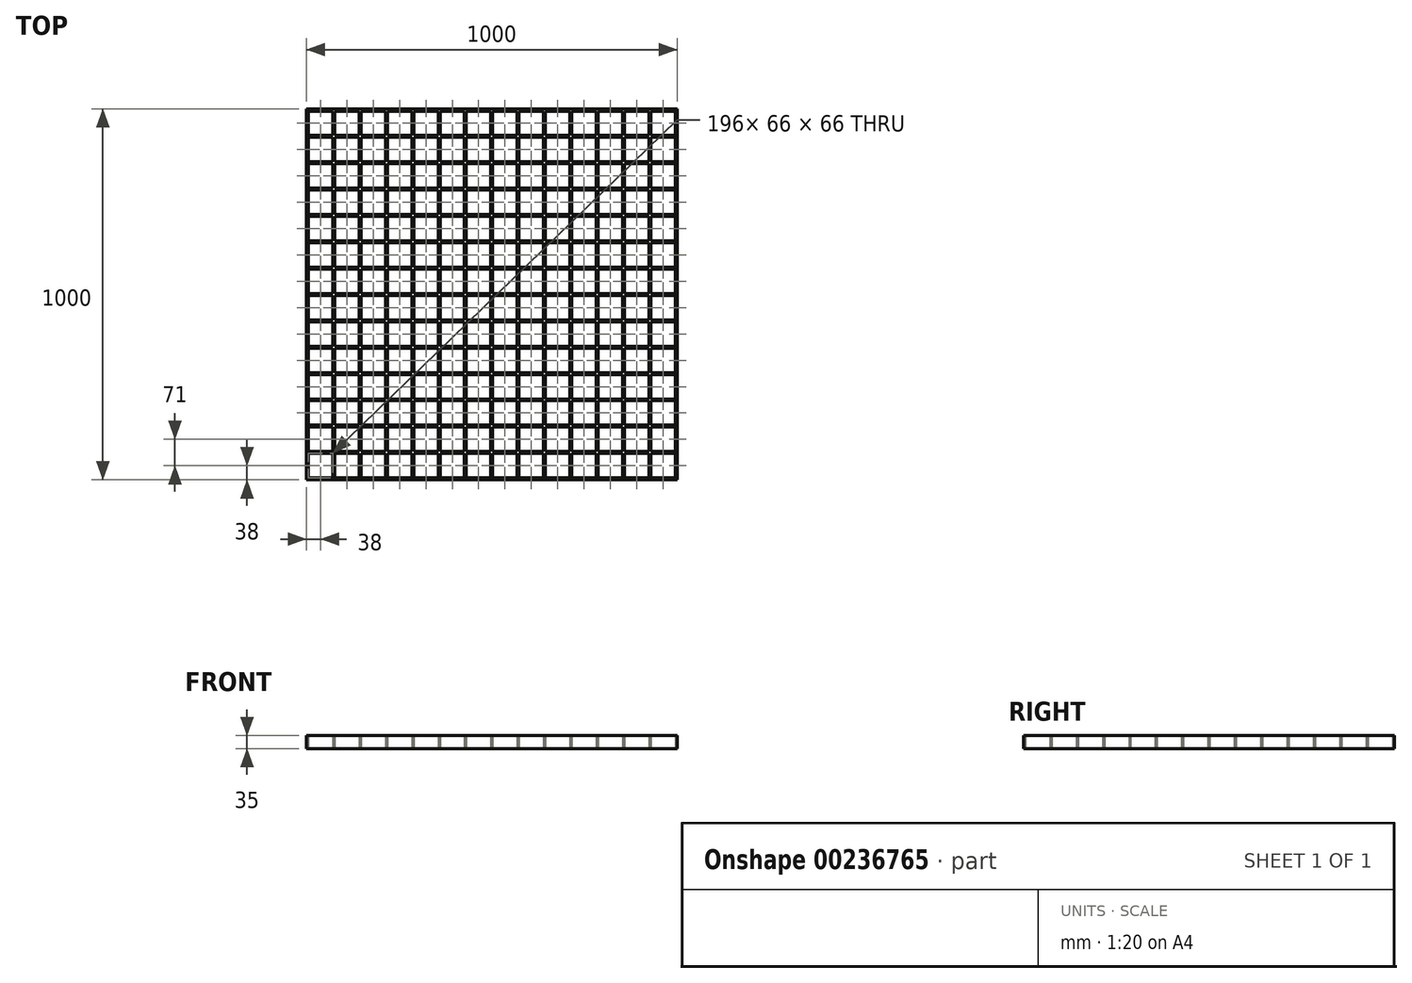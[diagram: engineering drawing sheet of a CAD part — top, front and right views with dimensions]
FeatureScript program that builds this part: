
annotation { "Feature Type Name" : "Feature", "Feature Type Description" : "" }
export const myFeature = defineFeature(function(context is Context, id is Id, definition is map)
    precondition{}
    {
        {
            var Q0;
            Q0=qCreatedBy(makeId("Top.planeOp"),FACE);
            var sketch = newSketch(context, id + "F0", { "sketchPlane" : qUnion([Q0])});
            skLineSegment(sketch, "E0.bottom", {"start": v(0, 0) * mm, "end": v(1000, 0) * mm});
            skLineSegment(sketch, "E0.top", {"start": v(0, 1000) * mm, "end": v(1000, 1000) * mm});
            skLineSegment(sketch, "E0.left", {"start": v(0, 0) * mm, "end": v(0, 1000) * mm});
            skLineSegment(sketch, "E0.right", {"start": v(1000, 0) * mm, "end": v(1000, 1000) * mm});
            skLineSegment(sketch, "E1.bottom", {"start": v(5, 5) * mm, "end": v(71, 5) * mm});
            skLineSegment(sketch, "E1.top", {"start": v(5, 71) * mm, "end": v(71, 71) * mm});
            skLineSegment(sketch, "E1.left", {"start": v(5, 5) * mm, "end": v(5, 71) * mm});
            skLineSegment(sketch, "E1.right", {"start": v(71, 5) * mm, "end": v(71, 71) * mm});
            skLineSegment(sketch, "E2.0.1.0", {"start": v(5, 142) * mm, "end": v(71, 142) * mm});
            skLineSegment(sketch, "E2.0.1.1", {"start": v(5, 76) * mm, "end": v(5, 142) * mm});
            skLineSegment(sketch, "E2.0.1.2", {"start": v(5, 76) * mm, "end": v(71, 76) * mm});
            skLineSegment(sketch, "E2.0.1.3", {"start": v(71, 76) * mm, "end": v(71, 142) * mm});
            skLineSegment(sketch, "E2.0.2.0", {"start": v(5, 213) * mm, "end": v(71, 213) * mm});
            skLineSegment(sketch, "E2.0.2.1", {"start": v(5, 147) * mm, "end": v(5, 213) * mm});
            skLineSegment(sketch, "E2.0.2.2", {"start": v(5, 147) * mm, "end": v(71, 147) * mm});
            skLineSegment(sketch, "E2.0.2.3", {"start": v(71, 147) * mm, "end": v(71, 213) * mm});
            skLineSegment(sketch, "E2.0.3.0", {"start": v(5, 284) * mm, "end": v(71, 284) * mm});
            skLineSegment(sketch, "E2.0.3.1", {"start": v(5, 218) * mm, "end": v(5, 284) * mm});
            skLineSegment(sketch, "E2.0.3.2", {"start": v(5, 218) * mm, "end": v(71, 218) * mm});
            skLineSegment(sketch, "E2.0.3.3", {"start": v(71, 218) * mm, "end": v(71, 284) * mm});
            skLineSegment(sketch, "E2.0.4.0", {"start": v(5, 355) * mm, "end": v(71, 355) * mm});
            skLineSegment(sketch, "E2.0.4.1", {"start": v(5, 289) * mm, "end": v(5, 355) * mm});
            skLineSegment(sketch, "E2.0.4.2", {"start": v(5, 289) * mm, "end": v(71, 289) * mm});
            skLineSegment(sketch, "E2.0.4.3", {"start": v(71, 289) * mm, "end": v(71, 355) * mm});
            skLineSegment(sketch, "E2.0.5.0", {"start": v(5, 426) * mm, "end": v(71, 426) * mm});
            skLineSegment(sketch, "E2.0.5.1", {"start": v(5, 360) * mm, "end": v(5, 426) * mm});
            skLineSegment(sketch, "E2.0.5.2", {"start": v(5, 360) * mm, "end": v(71, 360) * mm});
            skLineSegment(sketch, "E2.0.5.3", {"start": v(71, 360) * mm, "end": v(71, 426) * mm});
            skLineSegment(sketch, "E2.0.6.0", {"start": v(5, 497) * mm, "end": v(71, 497) * mm});
            skLineSegment(sketch, "E2.0.6.1", {"start": v(5, 431) * mm, "end": v(5, 497) * mm});
            skLineSegment(sketch, "E2.0.6.2", {"start": v(5, 431) * mm, "end": v(71, 431) * mm});
            skLineSegment(sketch, "E2.0.6.3", {"start": v(71, 431) * mm, "end": v(71, 497) * mm});
            skLineSegment(sketch, "E2.0.7.0", {"start": v(5, 568) * mm, "end": v(71, 568) * mm});
            skLineSegment(sketch, "E2.0.7.1", {"start": v(5, 502) * mm, "end": v(5, 568) * mm});
            skLineSegment(sketch, "E2.0.7.2", {"start": v(5, 502) * mm, "end": v(71, 502) * mm});
            skLineSegment(sketch, "E2.0.7.3", {"start": v(71, 502) * mm, "end": v(71, 568) * mm});
            skLineSegment(sketch, "E2.0.8.0", {"start": v(5, 639) * mm, "end": v(71, 639) * mm});
            skLineSegment(sketch, "E2.0.8.1", {"start": v(5, 573) * mm, "end": v(5, 639) * mm});
            skLineSegment(sketch, "E2.0.8.2", {"start": v(5, 573) * mm, "end": v(71, 573) * mm});
            skLineSegment(sketch, "E2.0.8.3", {"start": v(71, 573) * mm, "end": v(71, 639) * mm});
            skLineSegment(sketch, "E2.0.9.0", {"start": v(5, 710) * mm, "end": v(71, 710) * mm});
            skLineSegment(sketch, "E2.0.9.1", {"start": v(5, 644) * mm, "end": v(5, 710) * mm});
            skLineSegment(sketch, "E2.0.9.2", {"start": v(5, 644) * mm, "end": v(71, 644) * mm});
            skLineSegment(sketch, "E2.0.9.3", {"start": v(71, 644) * mm, "end": v(71, 710) * mm});
            skLineSegment(sketch, "E2.0.10.0", {"start": v(5, 781) * mm, "end": v(71, 781) * mm});
            skLineSegment(sketch, "E2.0.10.1", {"start": v(5, 715) * mm, "end": v(5, 781) * mm});
            skLineSegment(sketch, "E2.0.10.2", {"start": v(5, 715) * mm, "end": v(71, 715) * mm});
            skLineSegment(sketch, "E2.0.10.3", {"start": v(71, 715) * mm, "end": v(71, 781) * mm});
            skLineSegment(sketch, "E2.0.11.0", {"start": v(5, 852) * mm, "end": v(71, 852) * mm});
            skLineSegment(sketch, "E2.0.11.1", {"start": v(5, 786) * mm, "end": v(5, 852) * mm});
            skLineSegment(sketch, "E2.0.11.2", {"start": v(5, 786) * mm, "end": v(71, 786) * mm});
            skLineSegment(sketch, "E2.0.11.3", {"start": v(71, 786) * mm, "end": v(71, 852) * mm});
            skLineSegment(sketch, "E2.0.12.0", {"start": v(5, 923) * mm, "end": v(71, 923) * mm});
            skLineSegment(sketch, "E2.0.12.1", {"start": v(5, 857) * mm, "end": v(5, 923) * mm});
            skLineSegment(sketch, "E2.0.12.2", {"start": v(5, 857) * mm, "end": v(71, 857) * mm});
            skLineSegment(sketch, "E2.0.12.3", {"start": v(71, 857) * mm, "end": v(71, 923) * mm});
            skLineSegment(sketch, "E2.0.13.0", {"start": v(5, 994) * mm, "end": v(71, 994) * mm});
            skLineSegment(sketch, "E2.0.13.1", {"start": v(5, 928) * mm, "end": v(5, 994) * mm});
            skLineSegment(sketch, "E2.0.13.2", {"start": v(5, 928) * mm, "end": v(71, 928) * mm});
            skLineSegment(sketch, "E2.0.13.3", {"start": v(71, 928) * mm, "end": v(71, 994) * mm});
            skLineSegment(sketch, "E2.1.0.0", {"start": v(76, 71) * mm, "end": v(142, 71) * mm});
            skLineSegment(sketch, "E2.1.0.1", {"start": v(76, 5) * mm, "end": v(76, 71) * mm});
            skLineSegment(sketch, "E2.1.0.2", {"start": v(76, 5) * mm, "end": v(142, 5) * mm});
            skLineSegment(sketch, "E2.1.0.3", {"start": v(142, 5) * mm, "end": v(142, 71) * mm});
            skLineSegment(sketch, "E2.1.1.0", {"start": v(76, 142) * mm, "end": v(142, 142) * mm});
            skLineSegment(sketch, "E2.1.1.1", {"start": v(76, 76) * mm, "end": v(76, 142) * mm});
            skLineSegment(sketch, "E2.1.1.2", {"start": v(76, 76) * mm, "end": v(142, 76) * mm});
            skLineSegment(sketch, "E2.1.1.3", {"start": v(142, 76) * mm, "end": v(142, 142) * mm});
            skLineSegment(sketch, "E2.1.2.0", {"start": v(76, 213) * mm, "end": v(142, 213) * mm});
            skLineSegment(sketch, "E2.1.2.1", {"start": v(76, 147) * mm, "end": v(76, 213) * mm});
            skLineSegment(sketch, "E2.1.2.2", {"start": v(76, 147) * mm, "end": v(142, 147) * mm});
            skLineSegment(sketch, "E2.1.2.3", {"start": v(142, 147) * mm, "end": v(142, 213) * mm});
            skLineSegment(sketch, "E2.1.3.0", {"start": v(76, 284) * mm, "end": v(142, 284) * mm});
            skLineSegment(sketch, "E2.1.3.1", {"start": v(76, 218) * mm, "end": v(76, 284) * mm});
            skLineSegment(sketch, "E2.1.3.2", {"start": v(76, 218) * mm, "end": v(142, 218) * mm});
            skLineSegment(sketch, "E2.1.3.3", {"start": v(142, 218) * mm, "end": v(142, 284) * mm});
            skLineSegment(sketch, "E2.1.4.0", {"start": v(76, 355) * mm, "end": v(142, 355) * mm});
            skLineSegment(sketch, "E2.1.4.1", {"start": v(76, 289) * mm, "end": v(76, 355) * mm});
            skLineSegment(sketch, "E2.1.4.2", {"start": v(76, 289) * mm, "end": v(142, 289) * mm});
            skLineSegment(sketch, "E2.1.4.3", {"start": v(142, 289) * mm, "end": v(142, 355) * mm});
            skLineSegment(sketch, "E2.1.5.0", {"start": v(76, 426) * mm, "end": v(142, 426) * mm});
            skLineSegment(sketch, "E2.1.5.1", {"start": v(76, 360) * mm, "end": v(76, 426) * mm});
            skLineSegment(sketch, "E2.1.5.2", {"start": v(76, 360) * mm, "end": v(142, 360) * mm});
            skLineSegment(sketch, "E2.1.5.3", {"start": v(142, 360) * mm, "end": v(142, 426) * mm});
            skLineSegment(sketch, "E2.1.6.0", {"start": v(76, 497) * mm, "end": v(142, 497) * mm});
            skLineSegment(sketch, "E2.1.6.1", {"start": v(76, 431) * mm, "end": v(76, 497) * mm});
            skLineSegment(sketch, "E2.1.6.2", {"start": v(76, 431) * mm, "end": v(142, 431) * mm});
            skLineSegment(sketch, "E2.1.6.3", {"start": v(142, 431) * mm, "end": v(142, 497) * mm});
            skLineSegment(sketch, "E2.1.7.0", {"start": v(76, 568) * mm, "end": v(142, 568) * mm});
            skLineSegment(sketch, "E2.1.7.1", {"start": v(76, 502) * mm, "end": v(76, 568) * mm});
            skLineSegment(sketch, "E2.1.7.2", {"start": v(76, 502) * mm, "end": v(142, 502) * mm});
            skLineSegment(sketch, "E2.1.7.3", {"start": v(142, 502) * mm, "end": v(142, 568) * mm});
            skLineSegment(sketch, "E2.1.8.0", {"start": v(76, 639) * mm, "end": v(142, 639) * mm});
            skLineSegment(sketch, "E2.1.8.1", {"start": v(76, 573) * mm, "end": v(76, 639) * mm});
            skLineSegment(sketch, "E2.1.8.2", {"start": v(76, 573) * mm, "end": v(142, 573) * mm});
            skLineSegment(sketch, "E2.1.8.3", {"start": v(142, 573) * mm, "end": v(142, 639) * mm});
            skLineSegment(sketch, "E2.1.9.0", {"start": v(76, 710) * mm, "end": v(142, 710) * mm});
            skLineSegment(sketch, "E2.1.9.1", {"start": v(76, 644) * mm, "end": v(76, 710) * mm});
            skLineSegment(sketch, "E2.1.9.2", {"start": v(76, 644) * mm, "end": v(142, 644) * mm});
            skLineSegment(sketch, "E2.1.9.3", {"start": v(142, 644) * mm, "end": v(142, 710) * mm});
            skLineSegment(sketch, "E2.1.10.0", {"start": v(76, 781) * mm, "end": v(142, 781) * mm});
            skLineSegment(sketch, "E2.1.10.1", {"start": v(76, 715) * mm, "end": v(76, 781) * mm});
            skLineSegment(sketch, "E2.1.10.2", {"start": v(76, 715) * mm, "end": v(142, 715) * mm});
            skLineSegment(sketch, "E2.1.10.3", {"start": v(142, 715) * mm, "end": v(142, 781) * mm});
            skLineSegment(sketch, "E2.1.11.0", {"start": v(76, 852) * mm, "end": v(142, 852) * mm});
            skLineSegment(sketch, "E2.1.11.1", {"start": v(76, 786) * mm, "end": v(76, 852) * mm});
            skLineSegment(sketch, "E2.1.11.2", {"start": v(76, 786) * mm, "end": v(142, 786) * mm});
            skLineSegment(sketch, "E2.1.11.3", {"start": v(142, 786) * mm, "end": v(142, 852) * mm});
            skLineSegment(sketch, "E2.1.12.0", {"start": v(76, 923) * mm, "end": v(142, 923) * mm});
            skLineSegment(sketch, "E2.1.12.1", {"start": v(76, 857) * mm, "end": v(76, 923) * mm});
            skLineSegment(sketch, "E2.1.12.2", {"start": v(76, 857) * mm, "end": v(142, 857) * mm});
            skLineSegment(sketch, "E2.1.12.3", {"start": v(142, 857) * mm, "end": v(142, 923) * mm});
            skLineSegment(sketch, "E2.1.13.0", {"start": v(76, 994) * mm, "end": v(142, 994) * mm});
            skLineSegment(sketch, "E2.1.13.1", {"start": v(76, 928) * mm, "end": v(76, 994) * mm});
            skLineSegment(sketch, "E2.1.13.2", {"start": v(76, 928) * mm, "end": v(142, 928) * mm});
            skLineSegment(sketch, "E2.1.13.3", {"start": v(142, 928) * mm, "end": v(142, 994) * mm});
            skLineSegment(sketch, "E2.2.0.0", {"start": v(147, 71) * mm, "end": v(213, 71) * mm});
            skLineSegment(sketch, "E2.2.0.1", {"start": v(147, 5) * mm, "end": v(147, 71) * mm});
            skLineSegment(sketch, "E2.2.0.2", {"start": v(147, 5) * mm, "end": v(213, 5) * mm});
            skLineSegment(sketch, "E2.2.0.3", {"start": v(213, 5) * mm, "end": v(213, 71) * mm});
            skLineSegment(sketch, "E2.2.1.0", {"start": v(147, 142) * mm, "end": v(213, 142) * mm});
            skLineSegment(sketch, "E2.2.1.1", {"start": v(147, 76) * mm, "end": v(147, 142) * mm});
            skLineSegment(sketch, "E2.2.1.2", {"start": v(147, 76) * mm, "end": v(213, 76) * mm});
            skLineSegment(sketch, "E2.2.1.3", {"start": v(213, 76) * mm, "end": v(213, 142) * mm});
            skLineSegment(sketch, "E2.2.2.0", {"start": v(147, 213) * mm, "end": v(213, 213) * mm});
            skLineSegment(sketch, "E2.2.2.1", {"start": v(147, 147) * mm, "end": v(147, 213) * mm});
            skLineSegment(sketch, "E2.2.2.2", {"start": v(147, 147) * mm, "end": v(213, 147) * mm});
            skLineSegment(sketch, "E2.2.2.3", {"start": v(213, 147) * mm, "end": v(213, 213) * mm});
            skLineSegment(sketch, "E2.2.3.0", {"start": v(147, 284) * mm, "end": v(213, 284) * mm});
            skLineSegment(sketch, "E2.2.3.1", {"start": v(147, 218) * mm, "end": v(147, 284) * mm});
            skLineSegment(sketch, "E2.2.3.2", {"start": v(147, 218) * mm, "end": v(213, 218) * mm});
            skLineSegment(sketch, "E2.2.3.3", {"start": v(213, 218) * mm, "end": v(213, 284) * mm});
            skLineSegment(sketch, "E2.2.4.0", {"start": v(147, 355) * mm, "end": v(213, 355) * mm});
            skLineSegment(sketch, "E2.2.4.1", {"start": v(147, 289) * mm, "end": v(147, 355) * mm});
            skLineSegment(sketch, "E2.2.4.2", {"start": v(147, 289) * mm, "end": v(213, 289) * mm});
            skLineSegment(sketch, "E2.2.4.3", {"start": v(213, 289) * mm, "end": v(213, 355) * mm});
            skLineSegment(sketch, "E2.2.5.0", {"start": v(147, 426) * mm, "end": v(213, 426) * mm});
            skLineSegment(sketch, "E2.2.5.1", {"start": v(147, 360) * mm, "end": v(147, 426) * mm});
            skLineSegment(sketch, "E2.2.5.2", {"start": v(147, 360) * mm, "end": v(213, 360) * mm});
            skLineSegment(sketch, "E2.2.5.3", {"start": v(213, 360) * mm, "end": v(213, 426) * mm});
            skLineSegment(sketch, "E2.2.6.0", {"start": v(147, 497) * mm, "end": v(213, 497) * mm});
            skLineSegment(sketch, "E2.2.6.1", {"start": v(147, 431) * mm, "end": v(147, 497) * mm});
            skLineSegment(sketch, "E2.2.6.2", {"start": v(147, 431) * mm, "end": v(213, 431) * mm});
            skLineSegment(sketch, "E2.2.6.3", {"start": v(213, 431) * mm, "end": v(213, 497) * mm});
            skLineSegment(sketch, "E2.2.7.0", {"start": v(147, 568) * mm, "end": v(213, 568) * mm});
            skLineSegment(sketch, "E2.2.7.1", {"start": v(147, 502) * mm, "end": v(147, 568) * mm});
            skLineSegment(sketch, "E2.2.7.2", {"start": v(147, 502) * mm, "end": v(213, 502) * mm});
            skLineSegment(sketch, "E2.2.7.3", {"start": v(213, 502) * mm, "end": v(213, 568) * mm});
            skLineSegment(sketch, "E2.2.8.0", {"start": v(147, 639) * mm, "end": v(213, 639) * mm});
            skLineSegment(sketch, "E2.2.8.1", {"start": v(147, 573) * mm, "end": v(147, 639) * mm});
            skLineSegment(sketch, "E2.2.8.2", {"start": v(147, 573) * mm, "end": v(213, 573) * mm});
            skLineSegment(sketch, "E2.2.8.3", {"start": v(213, 573) * mm, "end": v(213, 639) * mm});
            skLineSegment(sketch, "E2.2.9.0", {"start": v(147, 710) * mm, "end": v(213, 710) * mm});
            skLineSegment(sketch, "E2.2.9.1", {"start": v(147, 644) * mm, "end": v(147, 710) * mm});
            skLineSegment(sketch, "E2.2.9.2", {"start": v(147, 644) * mm, "end": v(213, 644) * mm});
            skLineSegment(sketch, "E2.2.9.3", {"start": v(213, 644) * mm, "end": v(213, 710) * mm});
            skLineSegment(sketch, "E2.2.10.0", {"start": v(147, 781) * mm, "end": v(213, 781) * mm});
            skLineSegment(sketch, "E2.2.10.1", {"start": v(147, 715) * mm, "end": v(147, 781) * mm});
            skLineSegment(sketch, "E2.2.10.2", {"start": v(147, 715) * mm, "end": v(213, 715) * mm});
            skLineSegment(sketch, "E2.2.10.3", {"start": v(213, 715) * mm, "end": v(213, 781) * mm});
            skLineSegment(sketch, "E2.2.11.0", {"start": v(147, 852) * mm, "end": v(213, 852) * mm});
            skLineSegment(sketch, "E2.2.11.1", {"start": v(147, 786) * mm, "end": v(147, 852) * mm});
            skLineSegment(sketch, "E2.2.11.2", {"start": v(147, 786) * mm, "end": v(213, 786) * mm});
            skLineSegment(sketch, "E2.2.11.3", {"start": v(213, 786) * mm, "end": v(213, 852) * mm});
            skLineSegment(sketch, "E2.2.12.0", {"start": v(147, 923) * mm, "end": v(213, 923) * mm});
            skLineSegment(sketch, "E2.2.12.1", {"start": v(147, 857) * mm, "end": v(147, 923) * mm});
            skLineSegment(sketch, "E2.2.12.2", {"start": v(147, 857) * mm, "end": v(213, 857) * mm});
            skLineSegment(sketch, "E2.2.12.3", {"start": v(213, 857) * mm, "end": v(213, 923) * mm});
            skLineSegment(sketch, "E2.2.13.0", {"start": v(147, 994) * mm, "end": v(213, 994) * mm});
            skLineSegment(sketch, "E2.2.13.1", {"start": v(147, 928) * mm, "end": v(147, 994) * mm});
            skLineSegment(sketch, "E2.2.13.2", {"start": v(147, 928) * mm, "end": v(213, 928) * mm});
            skLineSegment(sketch, "E2.2.13.3", {"start": v(213, 928) * mm, "end": v(213, 994) * mm});
            skLineSegment(sketch, "E2.3.0.0", {"start": v(218, 71) * mm, "end": v(284, 71) * mm});
            skLineSegment(sketch, "E2.3.0.1", {"start": v(218, 5) * mm, "end": v(218, 71) * mm});
            skLineSegment(sketch, "E2.3.0.2", {"start": v(218, 5) * mm, "end": v(284, 5) * mm});
            skLineSegment(sketch, "E2.3.0.3", {"start": v(284, 5) * mm, "end": v(284, 71) * mm});
            skLineSegment(sketch, "E2.3.1.0", {"start": v(218, 142) * mm, "end": v(284, 142) * mm});
            skLineSegment(sketch, "E2.3.1.1", {"start": v(218, 76) * mm, "end": v(218, 142) * mm});
            skLineSegment(sketch, "E2.3.1.2", {"start": v(218, 76) * mm, "end": v(284, 76) * mm});
            skLineSegment(sketch, "E2.3.1.3", {"start": v(284, 76) * mm, "end": v(284, 142) * mm});
            skLineSegment(sketch, "E2.3.2.0", {"start": v(218, 213) * mm, "end": v(284, 213) * mm});
            skLineSegment(sketch, "E2.3.2.1", {"start": v(218, 147) * mm, "end": v(218, 213) * mm});
            skLineSegment(sketch, "E2.3.2.2", {"start": v(218, 147) * mm, "end": v(284, 147) * mm});
            skLineSegment(sketch, "E2.3.2.3", {"start": v(284, 147) * mm, "end": v(284, 213) * mm});
            skLineSegment(sketch, "E2.3.3.0", {"start": v(218, 284) * mm, "end": v(284, 284) * mm});
            skLineSegment(sketch, "E2.3.3.1", {"start": v(218, 218) * mm, "end": v(218, 284) * mm});
            skLineSegment(sketch, "E2.3.3.2", {"start": v(218, 218) * mm, "end": v(284, 218) * mm});
            skLineSegment(sketch, "E2.3.3.3", {"start": v(284, 218) * mm, "end": v(284, 284) * mm});
            skLineSegment(sketch, "E2.3.4.0", {"start": v(218, 355) * mm, "end": v(284, 355) * mm});
            skLineSegment(sketch, "E2.3.4.1", {"start": v(218, 289) * mm, "end": v(218, 355) * mm});
            skLineSegment(sketch, "E2.3.4.2", {"start": v(218, 289) * mm, "end": v(284, 289) * mm});
            skLineSegment(sketch, "E2.3.4.3", {"start": v(284, 289) * mm, "end": v(284, 355) * mm});
            skLineSegment(sketch, "E2.3.5.0", {"start": v(218, 426) * mm, "end": v(284, 426) * mm});
            skLineSegment(sketch, "E2.3.5.1", {"start": v(218, 360) * mm, "end": v(218, 426) * mm});
            skLineSegment(sketch, "E2.3.5.2", {"start": v(218, 360) * mm, "end": v(284, 360) * mm});
            skLineSegment(sketch, "E2.3.5.3", {"start": v(284, 360) * mm, "end": v(284, 426) * mm});
            skLineSegment(sketch, "E2.3.6.0", {"start": v(218, 497) * mm, "end": v(284, 497) * mm});
            skLineSegment(sketch, "E2.3.6.1", {"start": v(218, 431) * mm, "end": v(218, 497) * mm});
            skLineSegment(sketch, "E2.3.6.2", {"start": v(218, 431) * mm, "end": v(284, 431) * mm});
            skLineSegment(sketch, "E2.3.6.3", {"start": v(284, 431) * mm, "end": v(284, 497) * mm});
            skLineSegment(sketch, "E2.3.7.0", {"start": v(218, 568) * mm, "end": v(284, 568) * mm});
            skLineSegment(sketch, "E2.3.7.1", {"start": v(218, 502) * mm, "end": v(218, 568) * mm});
            skLineSegment(sketch, "E2.3.7.2", {"start": v(218, 502) * mm, "end": v(284, 502) * mm});
            skLineSegment(sketch, "E2.3.7.3", {"start": v(284, 502) * mm, "end": v(284, 568) * mm});
            skLineSegment(sketch, "E2.3.8.0", {"start": v(218, 639) * mm, "end": v(284, 639) * mm});
            skLineSegment(sketch, "E2.3.8.1", {"start": v(218, 573) * mm, "end": v(218, 639) * mm});
            skLineSegment(sketch, "E2.3.8.2", {"start": v(218, 573) * mm, "end": v(284, 573) * mm});
            skLineSegment(sketch, "E2.3.8.3", {"start": v(284, 573) * mm, "end": v(284, 639) * mm});
            skLineSegment(sketch, "E2.3.9.0", {"start": v(218, 710) * mm, "end": v(284, 710) * mm});
            skLineSegment(sketch, "E2.3.9.1", {"start": v(218, 644) * mm, "end": v(218, 710) * mm});
            skLineSegment(sketch, "E2.3.9.2", {"start": v(218, 644) * mm, "end": v(284, 644) * mm});
            skLineSegment(sketch, "E2.3.9.3", {"start": v(284, 644) * mm, "end": v(284, 710) * mm});
            skLineSegment(sketch, "E2.3.10.0", {"start": v(218, 781) * mm, "end": v(284, 781) * mm});
            skLineSegment(sketch, "E2.3.10.1", {"start": v(218, 715) * mm, "end": v(218, 781) * mm});
            skLineSegment(sketch, "E2.3.10.2", {"start": v(218, 715) * mm, "end": v(284, 715) * mm});
            skLineSegment(sketch, "E2.3.10.3", {"start": v(284, 715) * mm, "end": v(284, 781) * mm});
            skLineSegment(sketch, "E2.3.11.0", {"start": v(218, 852) * mm, "end": v(284, 852) * mm});
            skLineSegment(sketch, "E2.3.11.1", {"start": v(218, 786) * mm, "end": v(218, 852) * mm});
            skLineSegment(sketch, "E2.3.11.2", {"start": v(218, 786) * mm, "end": v(284, 786) * mm});
            skLineSegment(sketch, "E2.3.11.3", {"start": v(284, 786) * mm, "end": v(284, 852) * mm});
            skLineSegment(sketch, "E2.3.12.0", {"start": v(218, 923) * mm, "end": v(284, 923) * mm});
            skLineSegment(sketch, "E2.3.12.1", {"start": v(218, 857) * mm, "end": v(218, 923) * mm});
            skLineSegment(sketch, "E2.3.12.2", {"start": v(218, 857) * mm, "end": v(284, 857) * mm});
            skLineSegment(sketch, "E2.3.12.3", {"start": v(284, 857) * mm, "end": v(284, 923) * mm});
            skLineSegment(sketch, "E2.3.13.0", {"start": v(218, 994) * mm, "end": v(284, 994) * mm});
            skLineSegment(sketch, "E2.3.13.1", {"start": v(218, 928) * mm, "end": v(218, 994) * mm});
            skLineSegment(sketch, "E2.3.13.2", {"start": v(218, 928) * mm, "end": v(284, 928) * mm});
            skLineSegment(sketch, "E2.3.13.3", {"start": v(284, 928) * mm, "end": v(284, 994) * mm});
            skLineSegment(sketch, "E2.4.0.0", {"start": v(289, 71) * mm, "end": v(355, 71) * mm});
            skLineSegment(sketch, "E2.4.0.1", {"start": v(289, 5) * mm, "end": v(289, 71) * mm});
            skLineSegment(sketch, "E2.4.0.2", {"start": v(289, 5) * mm, "end": v(355, 5) * mm});
            skLineSegment(sketch, "E2.4.0.3", {"start": v(355, 5) * mm, "end": v(355, 71) * mm});
            skLineSegment(sketch, "E2.4.1.0", {"start": v(289, 142) * mm, "end": v(355, 142) * mm});
            skLineSegment(sketch, "E2.4.1.1", {"start": v(289, 76) * mm, "end": v(289, 142) * mm});
            skLineSegment(sketch, "E2.4.1.2", {"start": v(289, 76) * mm, "end": v(355, 76) * mm});
            skLineSegment(sketch, "E2.4.1.3", {"start": v(355, 76) * mm, "end": v(355, 142) * mm});
            skLineSegment(sketch, "E2.4.2.0", {"start": v(289, 213) * mm, "end": v(355, 213) * mm});
            skLineSegment(sketch, "E2.4.2.1", {"start": v(289, 147) * mm, "end": v(289, 213) * mm});
            skLineSegment(sketch, "E2.4.2.2", {"start": v(289, 147) * mm, "end": v(355, 147) * mm});
            skLineSegment(sketch, "E2.4.2.3", {"start": v(355, 147) * mm, "end": v(355, 213) * mm});
            skLineSegment(sketch, "E2.4.3.0", {"start": v(289, 284) * mm, "end": v(355, 284) * mm});
            skLineSegment(sketch, "E2.4.3.1", {"start": v(289, 218) * mm, "end": v(289, 284) * mm});
            skLineSegment(sketch, "E2.4.3.2", {"start": v(289, 218) * mm, "end": v(355, 218) * mm});
            skLineSegment(sketch, "E2.4.3.3", {"start": v(355, 218) * mm, "end": v(355, 284) * mm});
            skLineSegment(sketch, "E2.4.4.0", {"start": v(289, 355) * mm, "end": v(355, 355) * mm});
            skLineSegment(sketch, "E2.4.4.1", {"start": v(289, 289) * mm, "end": v(289, 355) * mm});
            skLineSegment(sketch, "E2.4.4.2", {"start": v(289, 289) * mm, "end": v(355, 289) * mm});
            skLineSegment(sketch, "E2.4.4.3", {"start": v(355, 289) * mm, "end": v(355, 355) * mm});
            skLineSegment(sketch, "E2.4.5.0", {"start": v(289, 426) * mm, "end": v(355, 426) * mm});
            skLineSegment(sketch, "E2.4.5.1", {"start": v(289, 360) * mm, "end": v(289, 426) * mm});
            skLineSegment(sketch, "E2.4.5.2", {"start": v(289, 360) * mm, "end": v(355, 360) * mm});
            skLineSegment(sketch, "E2.4.5.3", {"start": v(355, 360) * mm, "end": v(355, 426) * mm});
            skLineSegment(sketch, "E2.4.6.0", {"start": v(289, 497) * mm, "end": v(355, 497) * mm});
            skLineSegment(sketch, "E2.4.6.1", {"start": v(289, 431) * mm, "end": v(289, 497) * mm});
            skLineSegment(sketch, "E2.4.6.2", {"start": v(289, 431) * mm, "end": v(355, 431) * mm});
            skLineSegment(sketch, "E2.4.6.3", {"start": v(355, 431) * mm, "end": v(355, 497) * mm});
            skLineSegment(sketch, "E2.4.7.0", {"start": v(289, 568) * mm, "end": v(355, 568) * mm});
            skLineSegment(sketch, "E2.4.7.1", {"start": v(289, 502) * mm, "end": v(289, 568) * mm});
            skLineSegment(sketch, "E2.4.7.2", {"start": v(289, 502) * mm, "end": v(355, 502) * mm});
            skLineSegment(sketch, "E2.4.7.3", {"start": v(355, 502) * mm, "end": v(355, 568) * mm});
            skLineSegment(sketch, "E2.4.8.0", {"start": v(289, 639) * mm, "end": v(355, 639) * mm});
            skLineSegment(sketch, "E2.4.8.1", {"start": v(289, 573) * mm, "end": v(289, 639) * mm});
            skLineSegment(sketch, "E2.4.8.2", {"start": v(289, 573) * mm, "end": v(355, 573) * mm});
            skLineSegment(sketch, "E2.4.8.3", {"start": v(355, 573) * mm, "end": v(355, 639) * mm});
            skLineSegment(sketch, "E2.4.9.0", {"start": v(289, 710) * mm, "end": v(355, 710) * mm});
            skLineSegment(sketch, "E2.4.9.1", {"start": v(289, 644) * mm, "end": v(289, 710) * mm});
            skLineSegment(sketch, "E2.4.9.2", {"start": v(289, 644) * mm, "end": v(355, 644) * mm});
            skLineSegment(sketch, "E2.4.9.3", {"start": v(355, 644) * mm, "end": v(355, 710) * mm});
            skLineSegment(sketch, "E2.4.10.0", {"start": v(289, 781) * mm, "end": v(355, 781) * mm});
            skLineSegment(sketch, "E2.4.10.1", {"start": v(289, 715) * mm, "end": v(289, 781) * mm});
            skLineSegment(sketch, "E2.4.10.2", {"start": v(289, 715) * mm, "end": v(355, 715) * mm});
            skLineSegment(sketch, "E2.4.10.3", {"start": v(355, 715) * mm, "end": v(355, 781) * mm});
            skLineSegment(sketch, "E2.4.11.0", {"start": v(289, 852) * mm, "end": v(355, 852) * mm});
            skLineSegment(sketch, "E2.4.11.1", {"start": v(289, 786) * mm, "end": v(289, 852) * mm});
            skLineSegment(sketch, "E2.4.11.2", {"start": v(289, 786) * mm, "end": v(355, 786) * mm});
            skLineSegment(sketch, "E2.4.11.3", {"start": v(355, 786) * mm, "end": v(355, 852) * mm});
            skLineSegment(sketch, "E2.4.12.0", {"start": v(289, 923) * mm, "end": v(355, 923) * mm});
            skLineSegment(sketch, "E2.4.12.1", {"start": v(289, 857) * mm, "end": v(289, 923) * mm});
            skLineSegment(sketch, "E2.4.12.2", {"start": v(289, 857) * mm, "end": v(355, 857) * mm});
            skLineSegment(sketch, "E2.4.12.3", {"start": v(355, 857) * mm, "end": v(355, 923) * mm});
            skLineSegment(sketch, "E2.4.13.0", {"start": v(289, 994) * mm, "end": v(355, 994) * mm});
            skLineSegment(sketch, "E2.4.13.1", {"start": v(289, 928) * mm, "end": v(289, 994) * mm});
            skLineSegment(sketch, "E2.4.13.2", {"start": v(289, 928) * mm, "end": v(355, 928) * mm});
            skLineSegment(sketch, "E2.4.13.3", {"start": v(355, 928) * mm, "end": v(355, 994) * mm});
            skLineSegment(sketch, "E2.5.0.0", {"start": v(360, 71) * mm, "end": v(426, 71) * mm});
            skLineSegment(sketch, "E2.5.0.1", {"start": v(360, 5) * mm, "end": v(360, 71) * mm});
            skLineSegment(sketch, "E2.5.0.2", {"start": v(360, 5) * mm, "end": v(426, 5) * mm});
            skLineSegment(sketch, "E2.5.0.3", {"start": v(426, 5) * mm, "end": v(426, 71) * mm});
            skLineSegment(sketch, "E2.5.1.0", {"start": v(360, 142) * mm, "end": v(426, 142) * mm});
            skLineSegment(sketch, "E2.5.1.1", {"start": v(360, 76) * mm, "end": v(360, 142) * mm});
            skLineSegment(sketch, "E2.5.1.2", {"start": v(360, 76) * mm, "end": v(426, 76) * mm});
            skLineSegment(sketch, "E2.5.1.3", {"start": v(426, 76) * mm, "end": v(426, 142) * mm});
            skLineSegment(sketch, "E2.5.2.0", {"start": v(360, 213) * mm, "end": v(426, 213) * mm});
            skLineSegment(sketch, "E2.5.2.1", {"start": v(360, 147) * mm, "end": v(360, 213) * mm});
            skLineSegment(sketch, "E2.5.2.2", {"start": v(360, 147) * mm, "end": v(426, 147) * mm});
            skLineSegment(sketch, "E2.5.2.3", {"start": v(426, 147) * mm, "end": v(426, 213) * mm});
            skLineSegment(sketch, "E2.5.3.0", {"start": v(360, 284) * mm, "end": v(426, 284) * mm});
            skLineSegment(sketch, "E2.5.3.1", {"start": v(360, 218) * mm, "end": v(360, 284) * mm});
            skLineSegment(sketch, "E2.5.3.2", {"start": v(360, 218) * mm, "end": v(426, 218) * mm});
            skLineSegment(sketch, "E2.5.3.3", {"start": v(426, 218) * mm, "end": v(426, 284) * mm});
            skLineSegment(sketch, "E2.5.4.0", {"start": v(360, 355) * mm, "end": v(426, 355) * mm});
            skLineSegment(sketch, "E2.5.4.1", {"start": v(360, 289) * mm, "end": v(360, 355) * mm});
            skLineSegment(sketch, "E2.5.4.2", {"start": v(360, 289) * mm, "end": v(426, 289) * mm});
            skLineSegment(sketch, "E2.5.4.3", {"start": v(426, 289) * mm, "end": v(426, 355) * mm});
            skLineSegment(sketch, "E2.5.5.0", {"start": v(360, 426) * mm, "end": v(426, 426) * mm});
            skLineSegment(sketch, "E2.5.5.1", {"start": v(360, 360) * mm, "end": v(360, 426) * mm});
            skLineSegment(sketch, "E2.5.5.2", {"start": v(360, 360) * mm, "end": v(426, 360) * mm});
            skLineSegment(sketch, "E2.5.5.3", {"start": v(426, 360) * mm, "end": v(426, 426) * mm});
            skLineSegment(sketch, "E2.5.6.0", {"start": v(360, 497) * mm, "end": v(426, 497) * mm});
            skLineSegment(sketch, "E2.5.6.1", {"start": v(360, 431) * mm, "end": v(360, 497) * mm});
            skLineSegment(sketch, "E2.5.6.2", {"start": v(360, 431) * mm, "end": v(426, 431) * mm});
            skLineSegment(sketch, "E2.5.6.3", {"start": v(426, 431) * mm, "end": v(426, 497) * mm});
            skLineSegment(sketch, "E2.5.7.0", {"start": v(360, 568) * mm, "end": v(426, 568) * mm});
            skLineSegment(sketch, "E2.5.7.1", {"start": v(360, 502) * mm, "end": v(360, 568) * mm});
            skLineSegment(sketch, "E2.5.7.2", {"start": v(360, 502) * mm, "end": v(426, 502) * mm});
            skLineSegment(sketch, "E2.5.7.3", {"start": v(426, 502) * mm, "end": v(426, 568) * mm});
            skLineSegment(sketch, "E2.5.8.0", {"start": v(360, 639) * mm, "end": v(426, 639) * mm});
            skLineSegment(sketch, "E2.5.8.1", {"start": v(360, 573) * mm, "end": v(360, 639) * mm});
            skLineSegment(sketch, "E2.5.8.2", {"start": v(360, 573) * mm, "end": v(426, 573) * mm});
            skLineSegment(sketch, "E2.5.8.3", {"start": v(426, 573) * mm, "end": v(426, 639) * mm});
            skLineSegment(sketch, "E2.5.9.0", {"start": v(360, 710) * mm, "end": v(426, 710) * mm});
            skLineSegment(sketch, "E2.5.9.1", {"start": v(360, 644) * mm, "end": v(360, 710) * mm});
            skLineSegment(sketch, "E2.5.9.2", {"start": v(360, 644) * mm, "end": v(426, 644) * mm});
            skLineSegment(sketch, "E2.5.9.3", {"start": v(426, 644) * mm, "end": v(426, 710) * mm});
            skLineSegment(sketch, "E2.5.10.0", {"start": v(360, 781) * mm, "end": v(426, 781) * mm});
            skLineSegment(sketch, "E2.5.10.1", {"start": v(360, 715) * mm, "end": v(360, 781) * mm});
            skLineSegment(sketch, "E2.5.10.2", {"start": v(360, 715) * mm, "end": v(426, 715) * mm});
            skLineSegment(sketch, "E2.5.10.3", {"start": v(426, 715) * mm, "end": v(426, 781) * mm});
            skLineSegment(sketch, "E2.5.11.0", {"start": v(360, 852) * mm, "end": v(426, 852) * mm});
            skLineSegment(sketch, "E2.5.11.1", {"start": v(360, 786) * mm, "end": v(360, 852) * mm});
            skLineSegment(sketch, "E2.5.11.2", {"start": v(360, 786) * mm, "end": v(426, 786) * mm});
            skLineSegment(sketch, "E2.5.11.3", {"start": v(426, 786) * mm, "end": v(426, 852) * mm});
            skLineSegment(sketch, "E2.5.12.0", {"start": v(360, 923) * mm, "end": v(426, 923) * mm});
            skLineSegment(sketch, "E2.5.12.1", {"start": v(360, 857) * mm, "end": v(360, 923) * mm});
            skLineSegment(sketch, "E2.5.12.2", {"start": v(360, 857) * mm, "end": v(426, 857) * mm});
            skLineSegment(sketch, "E2.5.12.3", {"start": v(426, 857) * mm, "end": v(426, 923) * mm});
            skLineSegment(sketch, "E2.5.13.0", {"start": v(360, 994) * mm, "end": v(426, 994) * mm});
            skLineSegment(sketch, "E2.5.13.1", {"start": v(360, 928) * mm, "end": v(360, 994) * mm});
            skLineSegment(sketch, "E2.5.13.2", {"start": v(360, 928) * mm, "end": v(426, 928) * mm});
            skLineSegment(sketch, "E2.5.13.3", {"start": v(426, 928) * mm, "end": v(426, 994) * mm});
            skLineSegment(sketch, "E2.6.0.0", {"start": v(431, 71) * mm, "end": v(497, 71) * mm});
            skLineSegment(sketch, "E2.6.0.1", {"start": v(431, 5) * mm, "end": v(431, 71) * mm});
            skLineSegment(sketch, "E2.6.0.2", {"start": v(431, 5) * mm, "end": v(497, 5) * mm});
            skLineSegment(sketch, "E2.6.0.3", {"start": v(497, 5) * mm, "end": v(497, 71) * mm});
            skLineSegment(sketch, "E2.6.1.0", {"start": v(431, 142) * mm, "end": v(497, 142) * mm});
            skLineSegment(sketch, "E2.6.1.1", {"start": v(431, 76) * mm, "end": v(431, 142) * mm});
            skLineSegment(sketch, "E2.6.1.2", {"start": v(431, 76) * mm, "end": v(497, 76) * mm});
            skLineSegment(sketch, "E2.6.1.3", {"start": v(497, 76) * mm, "end": v(497, 142) * mm});
            skLineSegment(sketch, "E2.6.2.0", {"start": v(431, 213) * mm, "end": v(497, 213) * mm});
            skLineSegment(sketch, "E2.6.2.1", {"start": v(431, 147) * mm, "end": v(431, 213) * mm});
            skLineSegment(sketch, "E2.6.2.2", {"start": v(431, 147) * mm, "end": v(497, 147) * mm});
            skLineSegment(sketch, "E2.6.2.3", {"start": v(497, 147) * mm, "end": v(497, 213) * mm});
            skLineSegment(sketch, "E2.6.3.0", {"start": v(431, 284) * mm, "end": v(497, 284) * mm});
            skLineSegment(sketch, "E2.6.3.1", {"start": v(431, 218) * mm, "end": v(431, 284) * mm});
            skLineSegment(sketch, "E2.6.3.2", {"start": v(431, 218) * mm, "end": v(497, 218) * mm});
            skLineSegment(sketch, "E2.6.3.3", {"start": v(497, 218) * mm, "end": v(497, 284) * mm});
            skLineSegment(sketch, "E2.6.4.0", {"start": v(431, 355) * mm, "end": v(497, 355) * mm});
            skLineSegment(sketch, "E2.6.4.1", {"start": v(431, 289) * mm, "end": v(431, 355) * mm});
            skLineSegment(sketch, "E2.6.4.2", {"start": v(431, 289) * mm, "end": v(497, 289) * mm});
            skLineSegment(sketch, "E2.6.4.3", {"start": v(497, 289) * mm, "end": v(497, 355) * mm});
            skLineSegment(sketch, "E2.6.5.0", {"start": v(431, 426) * mm, "end": v(497, 426) * mm});
            skLineSegment(sketch, "E2.6.5.1", {"start": v(431, 360) * mm, "end": v(431, 426) * mm});
            skLineSegment(sketch, "E2.6.5.2", {"start": v(431, 360) * mm, "end": v(497, 360) * mm});
            skLineSegment(sketch, "E2.6.5.3", {"start": v(497, 360) * mm, "end": v(497, 426) * mm});
            skLineSegment(sketch, "E2.6.6.0", {"start": v(431, 497) * mm, "end": v(497, 497) * mm});
            skLineSegment(sketch, "E2.6.6.1", {"start": v(431, 431) * mm, "end": v(431, 497) * mm});
            skLineSegment(sketch, "E2.6.6.2", {"start": v(431, 431) * mm, "end": v(497, 431) * mm});
            skLineSegment(sketch, "E2.6.6.3", {"start": v(497, 431) * mm, "end": v(497, 497) * mm});
            skLineSegment(sketch, "E2.6.7.0", {"start": v(431, 568) * mm, "end": v(497, 568) * mm});
            skLineSegment(sketch, "E2.6.7.1", {"start": v(431, 502) * mm, "end": v(431, 568) * mm});
            skLineSegment(sketch, "E2.6.7.2", {"start": v(431, 502) * mm, "end": v(497, 502) * mm});
            skLineSegment(sketch, "E2.6.7.3", {"start": v(497, 502) * mm, "end": v(497, 568) * mm});
            skLineSegment(sketch, "E2.6.8.0", {"start": v(431, 639) * mm, "end": v(497, 639) * mm});
            skLineSegment(sketch, "E2.6.8.1", {"start": v(431, 573) * mm, "end": v(431, 639) * mm});
            skLineSegment(sketch, "E2.6.8.2", {"start": v(431, 573) * mm, "end": v(497, 573) * mm});
            skLineSegment(sketch, "E2.6.8.3", {"start": v(497, 573) * mm, "end": v(497, 639) * mm});
            skLineSegment(sketch, "E2.6.9.0", {"start": v(431, 710) * mm, "end": v(497, 710) * mm});
            skLineSegment(sketch, "E2.6.9.1", {"start": v(431, 644) * mm, "end": v(431, 710) * mm});
            skLineSegment(sketch, "E2.6.9.2", {"start": v(431, 644) * mm, "end": v(497, 644) * mm});
            skLineSegment(sketch, "E2.6.9.3", {"start": v(497, 644) * mm, "end": v(497, 710) * mm});
            skLineSegment(sketch, "E2.6.10.0", {"start": v(431, 781) * mm, "end": v(497, 781) * mm});
            skLineSegment(sketch, "E2.6.10.1", {"start": v(431, 715) * mm, "end": v(431, 781) * mm});
            skLineSegment(sketch, "E2.6.10.2", {"start": v(431, 715) * mm, "end": v(497, 715) * mm});
            skLineSegment(sketch, "E2.6.10.3", {"start": v(497, 715) * mm, "end": v(497, 781) * mm});
            skLineSegment(sketch, "E2.6.11.0", {"start": v(431, 852) * mm, "end": v(497, 852) * mm});
            skLineSegment(sketch, "E2.6.11.1", {"start": v(431, 786) * mm, "end": v(431, 852) * mm});
            skLineSegment(sketch, "E2.6.11.2", {"start": v(431, 786) * mm, "end": v(497, 786) * mm});
            skLineSegment(sketch, "E2.6.11.3", {"start": v(497, 786) * mm, "end": v(497, 852) * mm});
            skLineSegment(sketch, "E2.6.12.0", {"start": v(431, 923) * mm, "end": v(497, 923) * mm});
            skLineSegment(sketch, "E2.6.12.1", {"start": v(431, 857) * mm, "end": v(431, 923) * mm});
            skLineSegment(sketch, "E2.6.12.2", {"start": v(431, 857) * mm, "end": v(497, 857) * mm});
            skLineSegment(sketch, "E2.6.12.3", {"start": v(497, 857) * mm, "end": v(497, 923) * mm});
            skLineSegment(sketch, "E2.6.13.0", {"start": v(431, 994) * mm, "end": v(497, 994) * mm});
            skLineSegment(sketch, "E2.6.13.1", {"start": v(431, 928) * mm, "end": v(431, 994) * mm});
            skLineSegment(sketch, "E2.6.13.2", {"start": v(431, 928) * mm, "end": v(497, 928) * mm});
            skLineSegment(sketch, "E2.6.13.3", {"start": v(497, 928) * mm, "end": v(497, 994) * mm});
            skLineSegment(sketch, "E2.7.0.0", {"start": v(502, 71) * mm, "end": v(568, 71) * mm});
            skLineSegment(sketch, "E2.7.0.1", {"start": v(502, 5) * mm, "end": v(502, 71) * mm});
            skLineSegment(sketch, "E2.7.0.2", {"start": v(502, 5) * mm, "end": v(568, 5) * mm});
            skLineSegment(sketch, "E2.7.0.3", {"start": v(568, 5) * mm, "end": v(568, 71) * mm});
            skLineSegment(sketch, "E2.7.1.0", {"start": v(502, 142) * mm, "end": v(568, 142) * mm});
            skLineSegment(sketch, "E2.7.1.1", {"start": v(502, 76) * mm, "end": v(502, 142) * mm});
            skLineSegment(sketch, "E2.7.1.2", {"start": v(502, 76) * mm, "end": v(568, 76) * mm});
            skLineSegment(sketch, "E2.7.1.3", {"start": v(568, 76) * mm, "end": v(568, 142) * mm});
            skLineSegment(sketch, "E2.7.2.0", {"start": v(502, 213) * mm, "end": v(568, 213) * mm});
            skLineSegment(sketch, "E2.7.2.1", {"start": v(502, 147) * mm, "end": v(502, 213) * mm});
            skLineSegment(sketch, "E2.7.2.2", {"start": v(502, 147) * mm, "end": v(568, 147) * mm});
            skLineSegment(sketch, "E2.7.2.3", {"start": v(568, 147) * mm, "end": v(568, 213) * mm});
            skLineSegment(sketch, "E2.7.3.0", {"start": v(502, 284) * mm, "end": v(568, 284) * mm});
            skLineSegment(sketch, "E2.7.3.1", {"start": v(502, 218) * mm, "end": v(502, 284) * mm});
            skLineSegment(sketch, "E2.7.3.2", {"start": v(502, 218) * mm, "end": v(568, 218) * mm});
            skLineSegment(sketch, "E2.7.3.3", {"start": v(568, 218) * mm, "end": v(568, 284) * mm});
            skLineSegment(sketch, "E2.7.4.0", {"start": v(502, 355) * mm, "end": v(568, 355) * mm});
            skLineSegment(sketch, "E2.7.4.1", {"start": v(502, 289) * mm, "end": v(502, 355) * mm});
            skLineSegment(sketch, "E2.7.4.2", {"start": v(502, 289) * mm, "end": v(568, 289) * mm});
            skLineSegment(sketch, "E2.7.4.3", {"start": v(568, 289) * mm, "end": v(568, 355) * mm});
            skLineSegment(sketch, "E2.7.5.0", {"start": v(502, 426) * mm, "end": v(568, 426) * mm});
            skLineSegment(sketch, "E2.7.5.1", {"start": v(502, 360) * mm, "end": v(502, 426) * mm});
            skLineSegment(sketch, "E2.7.5.2", {"start": v(502, 360) * mm, "end": v(568, 360) * mm});
            skLineSegment(sketch, "E2.7.5.3", {"start": v(568, 360) * mm, "end": v(568, 426) * mm});
            skLineSegment(sketch, "E2.7.6.0", {"start": v(502, 497) * mm, "end": v(568, 497) * mm});
            skLineSegment(sketch, "E2.7.6.1", {"start": v(502, 431) * mm, "end": v(502, 497) * mm});
            skLineSegment(sketch, "E2.7.6.2", {"start": v(502, 431) * mm, "end": v(568, 431) * mm});
            skLineSegment(sketch, "E2.7.6.3", {"start": v(568, 431) * mm, "end": v(568, 497) * mm});
            skLineSegment(sketch, "E2.7.7.0", {"start": v(502, 568) * mm, "end": v(568, 568) * mm});
            skLineSegment(sketch, "E2.7.7.1", {"start": v(502, 502) * mm, "end": v(502, 568) * mm});
            skLineSegment(sketch, "E2.7.7.2", {"start": v(502, 502) * mm, "end": v(568, 502) * mm});
            skLineSegment(sketch, "E2.7.7.3", {"start": v(568, 502) * mm, "end": v(568, 568) * mm});
            skLineSegment(sketch, "E2.7.8.0", {"start": v(502, 639) * mm, "end": v(568, 639) * mm});
            skLineSegment(sketch, "E2.7.8.1", {"start": v(502, 573) * mm, "end": v(502, 639) * mm});
            skLineSegment(sketch, "E2.7.8.2", {"start": v(502, 573) * mm, "end": v(568, 573) * mm});
            skLineSegment(sketch, "E2.7.8.3", {"start": v(568, 573) * mm, "end": v(568, 639) * mm});
            skLineSegment(sketch, "E2.7.9.0", {"start": v(502, 710) * mm, "end": v(568, 710) * mm});
            skLineSegment(sketch, "E2.7.9.1", {"start": v(502, 644) * mm, "end": v(502, 710) * mm});
            skLineSegment(sketch, "E2.7.9.2", {"start": v(502, 644) * mm, "end": v(568, 644) * mm});
            skLineSegment(sketch, "E2.7.9.3", {"start": v(568, 644) * mm, "end": v(568, 710) * mm});
            skLineSegment(sketch, "E2.7.10.0", {"start": v(502, 781) * mm, "end": v(568, 781) * mm});
            skLineSegment(sketch, "E2.7.10.1", {"start": v(502, 715) * mm, "end": v(502, 781) * mm});
            skLineSegment(sketch, "E2.7.10.2", {"start": v(502, 715) * mm, "end": v(568, 715) * mm});
            skLineSegment(sketch, "E2.7.10.3", {"start": v(568, 715) * mm, "end": v(568, 781) * mm});
            skLineSegment(sketch, "E2.7.11.0", {"start": v(502, 852) * mm, "end": v(568, 852) * mm});
            skLineSegment(sketch, "E2.7.11.1", {"start": v(502, 786) * mm, "end": v(502, 852) * mm});
            skLineSegment(sketch, "E2.7.11.2", {"start": v(502, 786) * mm, "end": v(568, 786) * mm});
            skLineSegment(sketch, "E2.7.11.3", {"start": v(568, 786) * mm, "end": v(568, 852) * mm});
            skLineSegment(sketch, "E2.7.12.0", {"start": v(502, 923) * mm, "end": v(568, 923) * mm});
            skLineSegment(sketch, "E2.7.12.1", {"start": v(502, 857) * mm, "end": v(502, 923) * mm});
            skLineSegment(sketch, "E2.7.12.2", {"start": v(502, 857) * mm, "end": v(568, 857) * mm});
            skLineSegment(sketch, "E2.7.12.3", {"start": v(568, 857) * mm, "end": v(568, 923) * mm});
            skLineSegment(sketch, "E2.7.13.0", {"start": v(502, 994) * mm, "end": v(568, 994) * mm});
            skLineSegment(sketch, "E2.7.13.1", {"start": v(502, 928) * mm, "end": v(502, 994) * mm});
            skLineSegment(sketch, "E2.7.13.2", {"start": v(502, 928) * mm, "end": v(568, 928) * mm});
            skLineSegment(sketch, "E2.7.13.3", {"start": v(568, 928) * mm, "end": v(568, 994) * mm});
            skLineSegment(sketch, "E2.8.0.0", {"start": v(573, 71) * mm, "end": v(639, 71) * mm});
            skLineSegment(sketch, "E2.8.0.1", {"start": v(573, 5) * mm, "end": v(573, 71) * mm});
            skLineSegment(sketch, "E2.8.0.2", {"start": v(573, 5) * mm, "end": v(639, 5) * mm});
            skLineSegment(sketch, "E2.8.0.3", {"start": v(639, 5) * mm, "end": v(639, 71) * mm});
            skLineSegment(sketch, "E2.8.1.0", {"start": v(573, 142) * mm, "end": v(639, 142) * mm});
            skLineSegment(sketch, "E2.8.1.1", {"start": v(573, 76) * mm, "end": v(573, 142) * mm});
            skLineSegment(sketch, "E2.8.1.2", {"start": v(573, 76) * mm, "end": v(639, 76) * mm});
            skLineSegment(sketch, "E2.8.1.3", {"start": v(639, 76) * mm, "end": v(639, 142) * mm});
            skLineSegment(sketch, "E2.8.2.0", {"start": v(573, 213) * mm, "end": v(639, 213) * mm});
            skLineSegment(sketch, "E2.8.2.1", {"start": v(573, 147) * mm, "end": v(573, 213) * mm});
            skLineSegment(sketch, "E2.8.2.2", {"start": v(573, 147) * mm, "end": v(639, 147) * mm});
            skLineSegment(sketch, "E2.8.2.3", {"start": v(639, 147) * mm, "end": v(639, 213) * mm});
            skLineSegment(sketch, "E2.8.3.0", {"start": v(573, 284) * mm, "end": v(639, 284) * mm});
            skLineSegment(sketch, "E2.8.3.1", {"start": v(573, 218) * mm, "end": v(573, 284) * mm});
            skLineSegment(sketch, "E2.8.3.2", {"start": v(573, 218) * mm, "end": v(639, 218) * mm});
            skLineSegment(sketch, "E2.8.3.3", {"start": v(639, 218) * mm, "end": v(639, 284) * mm});
            skLineSegment(sketch, "E2.8.4.0", {"start": v(573, 355) * mm, "end": v(639, 355) * mm});
            skLineSegment(sketch, "E2.8.4.1", {"start": v(573, 289) * mm, "end": v(573, 355) * mm});
            skLineSegment(sketch, "E2.8.4.2", {"start": v(573, 289) * mm, "end": v(639, 289) * mm});
            skLineSegment(sketch, "E2.8.4.3", {"start": v(639, 289) * mm, "end": v(639, 355) * mm});
            skLineSegment(sketch, "E2.8.5.0", {"start": v(573, 426) * mm, "end": v(639, 426) * mm});
            skLineSegment(sketch, "E2.8.5.1", {"start": v(573, 360) * mm, "end": v(573, 426) * mm});
            skLineSegment(sketch, "E2.8.5.2", {"start": v(573, 360) * mm, "end": v(639, 360) * mm});
            skLineSegment(sketch, "E2.8.5.3", {"start": v(639, 360) * mm, "end": v(639, 426) * mm});
            skLineSegment(sketch, "E2.8.6.0", {"start": v(573, 497) * mm, "end": v(639, 497) * mm});
            skLineSegment(sketch, "E2.8.6.1", {"start": v(573, 431) * mm, "end": v(573, 497) * mm});
            skLineSegment(sketch, "E2.8.6.2", {"start": v(573, 431) * mm, "end": v(639, 431) * mm});
            skLineSegment(sketch, "E2.8.6.3", {"start": v(639, 431) * mm, "end": v(639, 497) * mm});
            skLineSegment(sketch, "E2.8.7.0", {"start": v(573, 568) * mm, "end": v(639, 568) * mm});
            skLineSegment(sketch, "E2.8.7.1", {"start": v(573, 502) * mm, "end": v(573, 568) * mm});
            skLineSegment(sketch, "E2.8.7.2", {"start": v(573, 502) * mm, "end": v(639, 502) * mm});
            skLineSegment(sketch, "E2.8.7.3", {"start": v(639, 502) * mm, "end": v(639, 568) * mm});
            skLineSegment(sketch, "E2.8.8.0", {"start": v(573, 639) * mm, "end": v(639, 639) * mm});
            skLineSegment(sketch, "E2.8.8.1", {"start": v(573, 573) * mm, "end": v(573, 639) * mm});
            skLineSegment(sketch, "E2.8.8.2", {"start": v(573, 573) * mm, "end": v(639, 573) * mm});
            skLineSegment(sketch, "E2.8.8.3", {"start": v(639, 573) * mm, "end": v(639, 639) * mm});
            skLineSegment(sketch, "E2.8.9.0", {"start": v(573, 710) * mm, "end": v(639, 710) * mm});
            skLineSegment(sketch, "E2.8.9.1", {"start": v(573, 644) * mm, "end": v(573, 710) * mm});
            skLineSegment(sketch, "E2.8.9.2", {"start": v(573, 644) * mm, "end": v(639, 644) * mm});
            skLineSegment(sketch, "E2.8.9.3", {"start": v(639, 644) * mm, "end": v(639, 710) * mm});
            skLineSegment(sketch, "E2.8.10.0", {"start": v(573, 781) * mm, "end": v(639, 781) * mm});
            skLineSegment(sketch, "E2.8.10.1", {"start": v(573, 715) * mm, "end": v(573, 781) * mm});
            skLineSegment(sketch, "E2.8.10.2", {"start": v(573, 715) * mm, "end": v(639, 715) * mm});
            skLineSegment(sketch, "E2.8.10.3", {"start": v(639, 715) * mm, "end": v(639, 781) * mm});
            skLineSegment(sketch, "E2.8.11.0", {"start": v(573, 852) * mm, "end": v(639, 852) * mm});
            skLineSegment(sketch, "E2.8.11.1", {"start": v(573, 786) * mm, "end": v(573, 852) * mm});
            skLineSegment(sketch, "E2.8.11.2", {"start": v(573, 786) * mm, "end": v(639, 786) * mm});
            skLineSegment(sketch, "E2.8.11.3", {"start": v(639, 786) * mm, "end": v(639, 852) * mm});
            skLineSegment(sketch, "E2.8.12.0", {"start": v(573, 923) * mm, "end": v(639, 923) * mm});
            skLineSegment(sketch, "E2.8.12.1", {"start": v(573, 857) * mm, "end": v(573, 923) * mm});
            skLineSegment(sketch, "E2.8.12.2", {"start": v(573, 857) * mm, "end": v(639, 857) * mm});
            skLineSegment(sketch, "E2.8.12.3", {"start": v(639, 857) * mm, "end": v(639, 923) * mm});
            skLineSegment(sketch, "E2.8.13.0", {"start": v(573, 994) * mm, "end": v(639, 994) * mm});
            skLineSegment(sketch, "E2.8.13.1", {"start": v(573, 928) * mm, "end": v(573, 994) * mm});
            skLineSegment(sketch, "E2.8.13.2", {"start": v(573, 928) * mm, "end": v(639, 928) * mm});
            skLineSegment(sketch, "E2.8.13.3", {"start": v(639, 928) * mm, "end": v(639, 994) * mm});
            skLineSegment(sketch, "E2.9.0.0", {"start": v(644, 71) * mm, "end": v(710, 71) * mm});
            skLineSegment(sketch, "E2.9.0.1", {"start": v(644, 5) * mm, "end": v(644, 71) * mm});
            skLineSegment(sketch, "E2.9.0.2", {"start": v(644, 5) * mm, "end": v(710, 5) * mm});
            skLineSegment(sketch, "E2.9.0.3", {"start": v(710, 5) * mm, "end": v(710, 71) * mm});
            skLineSegment(sketch, "E2.9.1.0", {"start": v(644, 142) * mm, "end": v(710, 142) * mm});
            skLineSegment(sketch, "E2.9.1.1", {"start": v(644, 76) * mm, "end": v(644, 142) * mm});
            skLineSegment(sketch, "E2.9.1.2", {"start": v(644, 76) * mm, "end": v(710, 76) * mm});
            skLineSegment(sketch, "E2.9.1.3", {"start": v(710, 76) * mm, "end": v(710, 142) * mm});
            skLineSegment(sketch, "E2.9.2.0", {"start": v(644, 213) * mm, "end": v(710, 213) * mm});
            skLineSegment(sketch, "E2.9.2.1", {"start": v(644, 147) * mm, "end": v(644, 213) * mm});
            skLineSegment(sketch, "E2.9.2.2", {"start": v(644, 147) * mm, "end": v(710, 147) * mm});
            skLineSegment(sketch, "E2.9.2.3", {"start": v(710, 147) * mm, "end": v(710, 213) * mm});
            skLineSegment(sketch, "E2.9.3.0", {"start": v(644, 284) * mm, "end": v(710, 284) * mm});
            skLineSegment(sketch, "E2.9.3.1", {"start": v(644, 218) * mm, "end": v(644, 284) * mm});
            skLineSegment(sketch, "E2.9.3.2", {"start": v(644, 218) * mm, "end": v(710, 218) * mm});
            skLineSegment(sketch, "E2.9.3.3", {"start": v(710, 218) * mm, "end": v(710, 284) * mm});
            skLineSegment(sketch, "E2.9.4.0", {"start": v(644, 355) * mm, "end": v(710, 355) * mm});
            skLineSegment(sketch, "E2.9.4.1", {"start": v(644, 289) * mm, "end": v(644, 355) * mm});
            skLineSegment(sketch, "E2.9.4.2", {"start": v(644, 289) * mm, "end": v(710, 289) * mm});
            skLineSegment(sketch, "E2.9.4.3", {"start": v(710, 289) * mm, "end": v(710, 355) * mm});
            skLineSegment(sketch, "E2.9.5.0", {"start": v(644, 426) * mm, "end": v(710, 426) * mm});
            skLineSegment(sketch, "E2.9.5.1", {"start": v(644, 360) * mm, "end": v(644, 426) * mm});
            skLineSegment(sketch, "E2.9.5.2", {"start": v(644, 360) * mm, "end": v(710, 360) * mm});
            skLineSegment(sketch, "E2.9.5.3", {"start": v(710, 360) * mm, "end": v(710, 426) * mm});
            skLineSegment(sketch, "E2.9.6.0", {"start": v(644, 497) * mm, "end": v(710, 497) * mm});
            skLineSegment(sketch, "E2.9.6.1", {"start": v(644, 431) * mm, "end": v(644, 497) * mm});
            skLineSegment(sketch, "E2.9.6.2", {"start": v(644, 431) * mm, "end": v(710, 431) * mm});
            skLineSegment(sketch, "E2.9.6.3", {"start": v(710, 431) * mm, "end": v(710, 497) * mm});
            skLineSegment(sketch, "E2.9.7.0", {"start": v(644, 568) * mm, "end": v(710, 568) * mm});
            skLineSegment(sketch, "E2.9.7.1", {"start": v(644, 502) * mm, "end": v(644, 568) * mm});
            skLineSegment(sketch, "E2.9.7.2", {"start": v(644, 502) * mm, "end": v(710, 502) * mm});
            skLineSegment(sketch, "E2.9.7.3", {"start": v(710, 502) * mm, "end": v(710, 568) * mm});
            skLineSegment(sketch, "E2.9.8.0", {"start": v(644, 639) * mm, "end": v(710, 639) * mm});
            skLineSegment(sketch, "E2.9.8.1", {"start": v(644, 573) * mm, "end": v(644, 639) * mm});
            skLineSegment(sketch, "E2.9.8.2", {"start": v(644, 573) * mm, "end": v(710, 573) * mm});
            skLineSegment(sketch, "E2.9.8.3", {"start": v(710, 573) * mm, "end": v(710, 639) * mm});
            skLineSegment(sketch, "E2.9.9.0", {"start": v(644, 710) * mm, "end": v(710, 710) * mm});
            skLineSegment(sketch, "E2.9.9.1", {"start": v(644, 644) * mm, "end": v(644, 710) * mm});
            skLineSegment(sketch, "E2.9.9.2", {"start": v(644, 644) * mm, "end": v(710, 644) * mm});
            skLineSegment(sketch, "E2.9.9.3", {"start": v(710, 644) * mm, "end": v(710, 710) * mm});
            skLineSegment(sketch, "E2.9.10.0", {"start": v(644, 781) * mm, "end": v(710, 781) * mm});
            skLineSegment(sketch, "E2.9.10.1", {"start": v(644, 715) * mm, "end": v(644, 781) * mm});
            skLineSegment(sketch, "E2.9.10.2", {"start": v(644, 715) * mm, "end": v(710, 715) * mm});
            skLineSegment(sketch, "E2.9.10.3", {"start": v(710, 715) * mm, "end": v(710, 781) * mm});
            skLineSegment(sketch, "E2.9.11.0", {"start": v(644, 852) * mm, "end": v(710, 852) * mm});
            skLineSegment(sketch, "E2.9.11.1", {"start": v(644, 786) * mm, "end": v(644, 852) * mm});
            skLineSegment(sketch, "E2.9.11.2", {"start": v(644, 786) * mm, "end": v(710, 786) * mm});
            skLineSegment(sketch, "E2.9.11.3", {"start": v(710, 786) * mm, "end": v(710, 852) * mm});
            skLineSegment(sketch, "E2.9.12.0", {"start": v(644, 923) * mm, "end": v(710, 923) * mm});
            skLineSegment(sketch, "E2.9.12.1", {"start": v(644, 857) * mm, "end": v(644, 923) * mm});
            skLineSegment(sketch, "E2.9.12.2", {"start": v(644, 857) * mm, "end": v(710, 857) * mm});
            skLineSegment(sketch, "E2.9.12.3", {"start": v(710, 857) * mm, "end": v(710, 923) * mm});
            skLineSegment(sketch, "E2.9.13.0", {"start": v(644, 994) * mm, "end": v(710, 994) * mm});
            skLineSegment(sketch, "E2.9.13.1", {"start": v(644, 928) * mm, "end": v(644, 994) * mm});
            skLineSegment(sketch, "E2.9.13.2", {"start": v(644, 928) * mm, "end": v(710, 928) * mm});
            skLineSegment(sketch, "E2.9.13.3", {"start": v(710, 928) * mm, "end": v(710, 994) * mm});
            skLineSegment(sketch, "E2.10.0.0", {"start": v(715, 71) * mm, "end": v(781, 71) * mm});
            skLineSegment(sketch, "E2.10.0.1", {"start": v(715, 5) * mm, "end": v(715, 71) * mm});
            skLineSegment(sketch, "E2.10.0.2", {"start": v(715, 5) * mm, "end": v(781, 5) * mm});
            skLineSegment(sketch, "E2.10.0.3", {"start": v(781, 5) * mm, "end": v(781, 71) * mm});
            skLineSegment(sketch, "E2.10.1.0", {"start": v(715, 142) * mm, "end": v(781, 142) * mm});
            skLineSegment(sketch, "E2.10.1.1", {"start": v(715, 76) * mm, "end": v(715, 142) * mm});
            skLineSegment(sketch, "E2.10.1.2", {"start": v(715, 76) * mm, "end": v(781, 76) * mm});
            skLineSegment(sketch, "E2.10.1.3", {"start": v(781, 76) * mm, "end": v(781, 142) * mm});
            skLineSegment(sketch, "E2.10.2.0", {"start": v(715, 213) * mm, "end": v(781, 213) * mm});
            skLineSegment(sketch, "E2.10.2.1", {"start": v(715, 147) * mm, "end": v(715, 213) * mm});
            skLineSegment(sketch, "E2.10.2.2", {"start": v(715, 147) * mm, "end": v(781, 147) * mm});
            skLineSegment(sketch, "E2.10.2.3", {"start": v(781, 147) * mm, "end": v(781, 213) * mm});
            skLineSegment(sketch, "E2.10.3.0", {"start": v(715, 284) * mm, "end": v(781, 284) * mm});
            skLineSegment(sketch, "E2.10.3.1", {"start": v(715, 218) * mm, "end": v(715, 284) * mm});
            skLineSegment(sketch, "E2.10.3.2", {"start": v(715, 218) * mm, "end": v(781, 218) * mm});
            skLineSegment(sketch, "E2.10.3.3", {"start": v(781, 218) * mm, "end": v(781, 284) * mm});
            skLineSegment(sketch, "E2.10.4.0", {"start": v(715, 355) * mm, "end": v(781, 355) * mm});
            skLineSegment(sketch, "E2.10.4.1", {"start": v(715, 289) * mm, "end": v(715, 355) * mm});
            skLineSegment(sketch, "E2.10.4.2", {"start": v(715, 289) * mm, "end": v(781, 289) * mm});
            skLineSegment(sketch, "E2.10.4.3", {"start": v(781, 289) * mm, "end": v(781, 355) * mm});
            skLineSegment(sketch, "E2.10.5.0", {"start": v(715, 426) * mm, "end": v(781, 426) * mm});
            skLineSegment(sketch, "E2.10.5.1", {"start": v(715, 360) * mm, "end": v(715, 426) * mm});
            skLineSegment(sketch, "E2.10.5.2", {"start": v(715, 360) * mm, "end": v(781, 360) * mm});
            skLineSegment(sketch, "E2.10.5.3", {"start": v(781, 360) * mm, "end": v(781, 426) * mm});
            skLineSegment(sketch, "E2.10.6.0", {"start": v(715, 497) * mm, "end": v(781, 497) * mm});
            skLineSegment(sketch, "E2.10.6.1", {"start": v(715, 431) * mm, "end": v(715, 497) * mm});
            skLineSegment(sketch, "E2.10.6.2", {"start": v(715, 431) * mm, "end": v(781, 431) * mm});
            skLineSegment(sketch, "E2.10.6.3", {"start": v(781, 431) * mm, "end": v(781, 497) * mm});
            skLineSegment(sketch, "E2.10.7.0", {"start": v(715, 568) * mm, "end": v(781, 568) * mm});
            skLineSegment(sketch, "E2.10.7.1", {"start": v(715, 502) * mm, "end": v(715, 568) * mm});
            skLineSegment(sketch, "E2.10.7.2", {"start": v(715, 502) * mm, "end": v(781, 502) * mm});
            skLineSegment(sketch, "E2.10.7.3", {"start": v(781, 502) * mm, "end": v(781, 568) * mm});
            skLineSegment(sketch, "E2.10.8.0", {"start": v(715, 639) * mm, "end": v(781, 639) * mm});
            skLineSegment(sketch, "E2.10.8.1", {"start": v(715, 573) * mm, "end": v(715, 639) * mm});
            skLineSegment(sketch, "E2.10.8.2", {"start": v(715, 573) * mm, "end": v(781, 573) * mm});
            skLineSegment(sketch, "E2.10.8.3", {"start": v(781, 573) * mm, "end": v(781, 639) * mm});
            skLineSegment(sketch, "E2.10.9.0", {"start": v(715, 710) * mm, "end": v(781, 710) * mm});
            skLineSegment(sketch, "E2.10.9.1", {"start": v(715, 644) * mm, "end": v(715, 710) * mm});
            skLineSegment(sketch, "E2.10.9.2", {"start": v(715, 644) * mm, "end": v(781, 644) * mm});
            skLineSegment(sketch, "E2.10.9.3", {"start": v(781, 644) * mm, "end": v(781, 710) * mm});
            skLineSegment(sketch, "E2.10.10.0", {"start": v(715, 781) * mm, "end": v(781, 781) * mm});
            skLineSegment(sketch, "E2.10.10.1", {"start": v(715, 715) * mm, "end": v(715, 781) * mm});
            skLineSegment(sketch, "E2.10.10.2", {"start": v(715, 715) * mm, "end": v(781, 715) * mm});
            skLineSegment(sketch, "E2.10.10.3", {"start": v(781, 715) * mm, "end": v(781, 781) * mm});
            skLineSegment(sketch, "E2.10.11.0", {"start": v(715, 852) * mm, "end": v(781, 852) * mm});
            skLineSegment(sketch, "E2.10.11.1", {"start": v(715, 786) * mm, "end": v(715, 852) * mm});
            skLineSegment(sketch, "E2.10.11.2", {"start": v(715, 786) * mm, "end": v(781, 786) * mm});
            skLineSegment(sketch, "E2.10.11.3", {"start": v(781, 786) * mm, "end": v(781, 852) * mm});
            skLineSegment(sketch, "E2.10.12.0", {"start": v(715, 923) * mm, "end": v(781, 923) * mm});
            skLineSegment(sketch, "E2.10.12.1", {"start": v(715, 857) * mm, "end": v(715, 923) * mm});
            skLineSegment(sketch, "E2.10.12.2", {"start": v(715, 857) * mm, "end": v(781, 857) * mm});
            skLineSegment(sketch, "E2.10.12.3", {"start": v(781, 857) * mm, "end": v(781, 923) * mm});
            skLineSegment(sketch, "E2.10.13.0", {"start": v(715, 994) * mm, "end": v(781, 994) * mm});
            skLineSegment(sketch, "E2.10.13.1", {"start": v(715, 928) * mm, "end": v(715, 994) * mm});
            skLineSegment(sketch, "E2.10.13.2", {"start": v(715, 928) * mm, "end": v(781, 928) * mm});
            skLineSegment(sketch, "E2.10.13.3", {"start": v(781, 928) * mm, "end": v(781, 994) * mm});
            skLineSegment(sketch, "E2.11.0.0", {"start": v(786, 71) * mm, "end": v(852, 71) * mm});
            skLineSegment(sketch, "E2.11.0.1", {"start": v(786, 5) * mm, "end": v(786, 71) * mm});
            skLineSegment(sketch, "E2.11.0.2", {"start": v(786, 5) * mm, "end": v(852, 5) * mm});
            skLineSegment(sketch, "E2.11.0.3", {"start": v(852, 5) * mm, "end": v(852, 71) * mm});
            skLineSegment(sketch, "E2.11.1.0", {"start": v(786, 142) * mm, "end": v(852, 142) * mm});
            skLineSegment(sketch, "E2.11.1.1", {"start": v(786, 76) * mm, "end": v(786, 142) * mm});
            skLineSegment(sketch, "E2.11.1.2", {"start": v(786, 76) * mm, "end": v(852, 76) * mm});
            skLineSegment(sketch, "E2.11.1.3", {"start": v(852, 76) * mm, "end": v(852, 142) * mm});
            skLineSegment(sketch, "E2.11.2.0", {"start": v(786, 213) * mm, "end": v(852, 213) * mm});
            skLineSegment(sketch, "E2.11.2.1", {"start": v(786, 147) * mm, "end": v(786, 213) * mm});
            skLineSegment(sketch, "E2.11.2.2", {"start": v(786, 147) * mm, "end": v(852, 147) * mm});
            skLineSegment(sketch, "E2.11.2.3", {"start": v(852, 147) * mm, "end": v(852, 213) * mm});
            skLineSegment(sketch, "E2.11.3.0", {"start": v(786, 284) * mm, "end": v(852, 284) * mm});
            skLineSegment(sketch, "E2.11.3.1", {"start": v(786, 218) * mm, "end": v(786, 284) * mm});
            skLineSegment(sketch, "E2.11.3.2", {"start": v(786, 218) * mm, "end": v(852, 218) * mm});
            skLineSegment(sketch, "E2.11.3.3", {"start": v(852, 218) * mm, "end": v(852, 284) * mm});
            skLineSegment(sketch, "E2.11.4.0", {"start": v(786, 355) * mm, "end": v(852, 355) * mm});
            skLineSegment(sketch, "E2.11.4.1", {"start": v(786, 289) * mm, "end": v(786, 355) * mm});
            skLineSegment(sketch, "E2.11.4.2", {"start": v(786, 289) * mm, "end": v(852, 289) * mm});
            skLineSegment(sketch, "E2.11.4.3", {"start": v(852, 289) * mm, "end": v(852, 355) * mm});
            skLineSegment(sketch, "E2.11.5.0", {"start": v(786, 426) * mm, "end": v(852, 426) * mm});
            skLineSegment(sketch, "E2.11.5.1", {"start": v(786, 360) * mm, "end": v(786, 426) * mm});
            skLineSegment(sketch, "E2.11.5.2", {"start": v(786, 360) * mm, "end": v(852, 360) * mm});
            skLineSegment(sketch, "E2.11.5.3", {"start": v(852, 360) * mm, "end": v(852, 426) * mm});
            skLineSegment(sketch, "E2.11.6.0", {"start": v(786, 497) * mm, "end": v(852, 497) * mm});
            skLineSegment(sketch, "E2.11.6.1", {"start": v(786, 431) * mm, "end": v(786, 497) * mm});
            skLineSegment(sketch, "E2.11.6.2", {"start": v(786, 431) * mm, "end": v(852, 431) * mm});
            skLineSegment(sketch, "E2.11.6.3", {"start": v(852, 431) * mm, "end": v(852, 497) * mm});
            skLineSegment(sketch, "E2.11.7.0", {"start": v(786, 568) * mm, "end": v(852, 568) * mm});
            skLineSegment(sketch, "E2.11.7.1", {"start": v(786, 502) * mm, "end": v(786, 568) * mm});
            skLineSegment(sketch, "E2.11.7.2", {"start": v(786, 502) * mm, "end": v(852, 502) * mm});
            skLineSegment(sketch, "E2.11.7.3", {"start": v(852, 502) * mm, "end": v(852, 568) * mm});
            skLineSegment(sketch, "E2.11.8.0", {"start": v(786, 639) * mm, "end": v(852, 639) * mm});
            skLineSegment(sketch, "E2.11.8.1", {"start": v(786, 573) * mm, "end": v(786, 639) * mm});
            skLineSegment(sketch, "E2.11.8.2", {"start": v(786, 573) * mm, "end": v(852, 573) * mm});
            skLineSegment(sketch, "E2.11.8.3", {"start": v(852, 573) * mm, "end": v(852, 639) * mm});
            skLineSegment(sketch, "E2.11.9.0", {"start": v(786, 710) * mm, "end": v(852, 710) * mm});
            skLineSegment(sketch, "E2.11.9.1", {"start": v(786, 644) * mm, "end": v(786, 710) * mm});
            skLineSegment(sketch, "E2.11.9.2", {"start": v(786, 644) * mm, "end": v(852, 644) * mm});
            skLineSegment(sketch, "E2.11.9.3", {"start": v(852, 644) * mm, "end": v(852, 710) * mm});
            skLineSegment(sketch, "E2.11.10.0", {"start": v(786, 781) * mm, "end": v(852, 781) * mm});
            skLineSegment(sketch, "E2.11.10.1", {"start": v(786, 715) * mm, "end": v(786, 781) * mm});
            skLineSegment(sketch, "E2.11.10.2", {"start": v(786, 715) * mm, "end": v(852, 715) * mm});
            skLineSegment(sketch, "E2.11.10.3", {"start": v(852, 715) * mm, "end": v(852, 781) * mm});
            skLineSegment(sketch, "E2.11.11.0", {"start": v(786, 852) * mm, "end": v(852, 852) * mm});
            skLineSegment(sketch, "E2.11.11.1", {"start": v(786, 786) * mm, "end": v(786, 852) * mm});
            skLineSegment(sketch, "E2.11.11.2", {"start": v(786, 786) * mm, "end": v(852, 786) * mm});
            skLineSegment(sketch, "E2.11.11.3", {"start": v(852, 786) * mm, "end": v(852, 852) * mm});
            skLineSegment(sketch, "E2.11.12.0", {"start": v(786, 923) * mm, "end": v(852, 923) * mm});
            skLineSegment(sketch, "E2.11.12.1", {"start": v(786, 857) * mm, "end": v(786, 923) * mm});
            skLineSegment(sketch, "E2.11.12.2", {"start": v(786, 857) * mm, "end": v(852, 857) * mm});
            skLineSegment(sketch, "E2.11.12.3", {"start": v(852, 857) * mm, "end": v(852, 923) * mm});
            skLineSegment(sketch, "E2.11.13.0", {"start": v(786, 994) * mm, "end": v(852, 994) * mm});
            skLineSegment(sketch, "E2.11.13.1", {"start": v(786, 928) * mm, "end": v(786, 994) * mm});
            skLineSegment(sketch, "E2.11.13.2", {"start": v(786, 928) * mm, "end": v(852, 928) * mm});
            skLineSegment(sketch, "E2.11.13.3", {"start": v(852, 928) * mm, "end": v(852, 994) * mm});
            skLineSegment(sketch, "E2.12.0.0", {"start": v(857, 71) * mm, "end": v(923, 71) * mm});
            skLineSegment(sketch, "E2.12.0.1", {"start": v(857, 5) * mm, "end": v(857, 71) * mm});
            skLineSegment(sketch, "E2.12.0.2", {"start": v(857, 5) * mm, "end": v(923, 5) * mm});
            skLineSegment(sketch, "E2.12.0.3", {"start": v(923, 5) * mm, "end": v(923, 71) * mm});
            skLineSegment(sketch, "E2.12.1.0", {"start": v(857, 142) * mm, "end": v(923, 142) * mm});
            skLineSegment(sketch, "E2.12.1.1", {"start": v(857, 76) * mm, "end": v(857, 142) * mm});
            skLineSegment(sketch, "E2.12.1.2", {"start": v(857, 76) * mm, "end": v(923, 76) * mm});
            skLineSegment(sketch, "E2.12.1.3", {"start": v(923, 76) * mm, "end": v(923, 142) * mm});
            skLineSegment(sketch, "E2.12.2.0", {"start": v(857, 213) * mm, "end": v(923, 213) * mm});
            skLineSegment(sketch, "E2.12.2.1", {"start": v(857, 147) * mm, "end": v(857, 213) * mm});
            skLineSegment(sketch, "E2.12.2.2", {"start": v(857, 147) * mm, "end": v(923, 147) * mm});
            skLineSegment(sketch, "E2.12.2.3", {"start": v(923, 147) * mm, "end": v(923, 213) * mm});
            skLineSegment(sketch, "E2.12.3.0", {"start": v(857, 284) * mm, "end": v(923, 284) * mm});
            skLineSegment(sketch, "E2.12.3.1", {"start": v(857, 218) * mm, "end": v(857, 284) * mm});
            skLineSegment(sketch, "E2.12.3.2", {"start": v(857, 218) * mm, "end": v(923, 218) * mm});
            skLineSegment(sketch, "E2.12.3.3", {"start": v(923, 218) * mm, "end": v(923, 284) * mm});
            skLineSegment(sketch, "E2.12.4.0", {"start": v(857, 355) * mm, "end": v(923, 355) * mm});
            skLineSegment(sketch, "E2.12.4.1", {"start": v(857, 289) * mm, "end": v(857, 355) * mm});
            skLineSegment(sketch, "E2.12.4.2", {"start": v(857, 289) * mm, "end": v(923, 289) * mm});
            skLineSegment(sketch, "E2.12.4.3", {"start": v(923, 289) * mm, "end": v(923, 355) * mm});
            skLineSegment(sketch, "E2.12.5.0", {"start": v(857, 426) * mm, "end": v(923, 426) * mm});
            skLineSegment(sketch, "E2.12.5.1", {"start": v(857, 360) * mm, "end": v(857, 426) * mm});
            skLineSegment(sketch, "E2.12.5.2", {"start": v(857, 360) * mm, "end": v(923, 360) * mm});
            skLineSegment(sketch, "E2.12.5.3", {"start": v(923, 360) * mm, "end": v(923, 426) * mm});
            skLineSegment(sketch, "E2.12.6.0", {"start": v(857, 497) * mm, "end": v(923, 497) * mm});
            skLineSegment(sketch, "E2.12.6.1", {"start": v(857, 431) * mm, "end": v(857, 497) * mm});
            skLineSegment(sketch, "E2.12.6.2", {"start": v(857, 431) * mm, "end": v(923, 431) * mm});
            skLineSegment(sketch, "E2.12.6.3", {"start": v(923, 431) * mm, "end": v(923, 497) * mm});
            skLineSegment(sketch, "E2.12.7.0", {"start": v(857, 568) * mm, "end": v(923, 568) * mm});
            skLineSegment(sketch, "E2.12.7.1", {"start": v(857, 502) * mm, "end": v(857, 568) * mm});
            skLineSegment(sketch, "E2.12.7.2", {"start": v(857, 502) * mm, "end": v(923, 502) * mm});
            skLineSegment(sketch, "E2.12.7.3", {"start": v(923, 502) * mm, "end": v(923, 568) * mm});
            skLineSegment(sketch, "E2.12.8.0", {"start": v(857, 639) * mm, "end": v(923, 639) * mm});
            skLineSegment(sketch, "E2.12.8.1", {"start": v(857, 573) * mm, "end": v(857, 639) * mm});
            skLineSegment(sketch, "E2.12.8.2", {"start": v(857, 573) * mm, "end": v(923, 573) * mm});
            skLineSegment(sketch, "E2.12.8.3", {"start": v(923, 573) * mm, "end": v(923, 639) * mm});
            skLineSegment(sketch, "E2.12.9.0", {"start": v(857, 710) * mm, "end": v(923, 710) * mm});
            skLineSegment(sketch, "E2.12.9.1", {"start": v(857, 644) * mm, "end": v(857, 710) * mm});
            skLineSegment(sketch, "E2.12.9.2", {"start": v(857, 644) * mm, "end": v(923, 644) * mm});
            skLineSegment(sketch, "E2.12.9.3", {"start": v(923, 644) * mm, "end": v(923, 710) * mm});
            skLineSegment(sketch, "E2.12.10.0", {"start": v(857, 781) * mm, "end": v(923, 781) * mm});
            skLineSegment(sketch, "E2.12.10.1", {"start": v(857, 715) * mm, "end": v(857, 781) * mm});
            skLineSegment(sketch, "E2.12.10.2", {"start": v(857, 715) * mm, "end": v(923, 715) * mm});
            skLineSegment(sketch, "E2.12.10.3", {"start": v(923, 715) * mm, "end": v(923, 781) * mm});
            skLineSegment(sketch, "E2.12.11.0", {"start": v(857, 852) * mm, "end": v(923, 852) * mm});
            skLineSegment(sketch, "E2.12.11.1", {"start": v(857, 786) * mm, "end": v(857, 852) * mm});
            skLineSegment(sketch, "E2.12.11.2", {"start": v(857, 786) * mm, "end": v(923, 786) * mm});
            skLineSegment(sketch, "E2.12.11.3", {"start": v(923, 786) * mm, "end": v(923, 852) * mm});
            skLineSegment(sketch, "E2.12.12.0", {"start": v(857, 923) * mm, "end": v(923, 923) * mm});
            skLineSegment(sketch, "E2.12.12.1", {"start": v(857, 857) * mm, "end": v(857, 923) * mm});
            skLineSegment(sketch, "E2.12.12.2", {"start": v(857, 857) * mm, "end": v(923, 857) * mm});
            skLineSegment(sketch, "E2.12.12.3", {"start": v(923, 857) * mm, "end": v(923, 923) * mm});
            skLineSegment(sketch, "E2.12.13.0", {"start": v(857, 994) * mm, "end": v(923, 994) * mm});
            skLineSegment(sketch, "E2.12.13.1", {"start": v(857, 928) * mm, "end": v(857, 994) * mm});
            skLineSegment(sketch, "E2.12.13.2", {"start": v(857, 928) * mm, "end": v(923, 928) * mm});
            skLineSegment(sketch, "E2.12.13.3", {"start": v(923, 928) * mm, "end": v(923, 994) * mm});
            skLineSegment(sketch, "E2.13.0.0", {"start": v(928, 71) * mm, "end": v(994, 71) * mm});
            skLineSegment(sketch, "E2.13.0.1", {"start": v(928, 5) * mm, "end": v(928, 71) * mm});
            skLineSegment(sketch, "E2.13.0.2", {"start": v(928, 5) * mm, "end": v(994, 5) * mm});
            skLineSegment(sketch, "E2.13.0.3", {"start": v(994, 5) * mm, "end": v(994, 71) * mm});
            skLineSegment(sketch, "E2.13.1.0", {"start": v(928, 142) * mm, "end": v(994, 142) * mm});
            skLineSegment(sketch, "E2.13.1.1", {"start": v(928, 76) * mm, "end": v(928, 142) * mm});
            skLineSegment(sketch, "E2.13.1.2", {"start": v(928, 76) * mm, "end": v(994, 76) * mm});
            skLineSegment(sketch, "E2.13.1.3", {"start": v(994, 76) * mm, "end": v(994, 142) * mm});
            skLineSegment(sketch, "E2.13.2.0", {"start": v(928, 213) * mm, "end": v(994, 213) * mm});
            skLineSegment(sketch, "E2.13.2.1", {"start": v(928, 147) * mm, "end": v(928, 213) * mm});
            skLineSegment(sketch, "E2.13.2.2", {"start": v(928, 147) * mm, "end": v(994, 147) * mm});
            skLineSegment(sketch, "E2.13.2.3", {"start": v(994, 147) * mm, "end": v(994, 213) * mm});
            skLineSegment(sketch, "E2.13.3.0", {"start": v(928, 284) * mm, "end": v(994, 284) * mm});
            skLineSegment(sketch, "E2.13.3.1", {"start": v(928, 218) * mm, "end": v(928, 284) * mm});
            skLineSegment(sketch, "E2.13.3.2", {"start": v(928, 218) * mm, "end": v(994, 218) * mm});
            skLineSegment(sketch, "E2.13.3.3", {"start": v(994, 218) * mm, "end": v(994, 284) * mm});
            skLineSegment(sketch, "E2.13.4.0", {"start": v(928, 355) * mm, "end": v(994, 355) * mm});
            skLineSegment(sketch, "E2.13.4.1", {"start": v(928, 289) * mm, "end": v(928, 355) * mm});
            skLineSegment(sketch, "E2.13.4.2", {"start": v(928, 289) * mm, "end": v(994, 289) * mm});
            skLineSegment(sketch, "E2.13.4.3", {"start": v(994, 289) * mm, "end": v(994, 355) * mm});
            skLineSegment(sketch, "E2.13.5.0", {"start": v(928, 426) * mm, "end": v(994, 426) * mm});
            skLineSegment(sketch, "E2.13.5.1", {"start": v(928, 360) * mm, "end": v(928, 426) * mm});
            skLineSegment(sketch, "E2.13.5.2", {"start": v(928, 360) * mm, "end": v(994, 360) * mm});
            skLineSegment(sketch, "E2.13.5.3", {"start": v(994, 360) * mm, "end": v(994, 426) * mm});
            skLineSegment(sketch, "E2.13.6.0", {"start": v(928, 497) * mm, "end": v(994, 497) * mm});
            skLineSegment(sketch, "E2.13.6.1", {"start": v(928, 431) * mm, "end": v(928, 497) * mm});
            skLineSegment(sketch, "E2.13.6.2", {"start": v(928, 431) * mm, "end": v(994, 431) * mm});
            skLineSegment(sketch, "E2.13.6.3", {"start": v(994, 431) * mm, "end": v(994, 497) * mm});
            skLineSegment(sketch, "E2.13.7.0", {"start": v(928, 568) * mm, "end": v(994, 568) * mm});
            skLineSegment(sketch, "E2.13.7.1", {"start": v(928, 502) * mm, "end": v(928, 568) * mm});
            skLineSegment(sketch, "E2.13.7.2", {"start": v(928, 502) * mm, "end": v(994, 502) * mm});
            skLineSegment(sketch, "E2.13.7.3", {"start": v(994, 502) * mm, "end": v(994, 568) * mm});
            skLineSegment(sketch, "E2.13.8.0", {"start": v(928, 639) * mm, "end": v(994, 639) * mm});
            skLineSegment(sketch, "E2.13.8.1", {"start": v(928, 573) * mm, "end": v(928, 639) * mm});
            skLineSegment(sketch, "E2.13.8.2", {"start": v(928, 573) * mm, "end": v(994, 573) * mm});
            skLineSegment(sketch, "E2.13.8.3", {"start": v(994, 573) * mm, "end": v(994, 639) * mm});
            skLineSegment(sketch, "E2.13.9.0", {"start": v(928, 710) * mm, "end": v(994, 710) * mm});
            skLineSegment(sketch, "E2.13.9.1", {"start": v(928, 644) * mm, "end": v(928, 710) * mm});
            skLineSegment(sketch, "E2.13.9.2", {"start": v(928, 644) * mm, "end": v(994, 644) * mm});
            skLineSegment(sketch, "E2.13.9.3", {"start": v(994, 644) * mm, "end": v(994, 710) * mm});
            skLineSegment(sketch, "E2.13.10.0", {"start": v(928, 781) * mm, "end": v(994, 781) * mm});
            skLineSegment(sketch, "E2.13.10.1", {"start": v(928, 715) * mm, "end": v(928, 781) * mm});
            skLineSegment(sketch, "E2.13.10.2", {"start": v(928, 715) * mm, "end": v(994, 715) * mm});
            skLineSegment(sketch, "E2.13.10.3", {"start": v(994, 715) * mm, "end": v(994, 781) * mm});
            skLineSegment(sketch, "E2.13.11.0", {"start": v(928, 852) * mm, "end": v(994, 852) * mm});
            skLineSegment(sketch, "E2.13.11.1", {"start": v(928, 786) * mm, "end": v(928, 852) * mm});
            skLineSegment(sketch, "E2.13.11.2", {"start": v(928, 786) * mm, "end": v(994, 786) * mm});
            skLineSegment(sketch, "E2.13.11.3", {"start": v(994, 786) * mm, "end": v(994, 852) * mm});
            skLineSegment(sketch, "E2.13.12.0", {"start": v(928, 923) * mm, "end": v(994, 923) * mm});
            skLineSegment(sketch, "E2.13.12.1", {"start": v(928, 857) * mm, "end": v(928, 923) * mm});
            skLineSegment(sketch, "E2.13.12.2", {"start": v(928, 857) * mm, "end": v(994, 857) * mm});
            skLineSegment(sketch, "E2.13.12.3", {"start": v(994, 857) * mm, "end": v(994, 923) * mm});
            skLineSegment(sketch, "E2.13.13.0", {"start": v(928, 994) * mm, "end": v(994, 994) * mm});
            skLineSegment(sketch, "E2.13.13.1", {"start": v(928, 928) * mm, "end": v(928, 994) * mm});
            skLineSegment(sketch, "E2.13.13.2", {"start": v(928, 928) * mm, "end": v(994, 928) * mm});
            skLineSegment(sketch, "E2.13.13.3", {"start": v(994, 928) * mm, "end": v(994, 994) * mm});
            skLineSegment(sketch, "E2.direction1", {"start": v(5, 71) * mm, "end": v(76, 71) * mm, "construction": true});
            skLineSegment(sketch, "E2.direction2", {"start": v(5, 71) * mm, "end": v(5, 142) * mm, "construction": true});
            skSolve(sketch);
        }
        {
            var Q0;
            Q0=makeQuery(id+"F0.imprint","IMPRINT",FACE,{"disambiguationData":[TD([[makeQuery(id+"F0.imprint","IMPRINT",EDGE,{"derivedFrom":sQuery(id+"F0.wireOp",EDGE,"E0.bottom")}),1.0]])]});
            extrude(context, id + "F1", {"entities" : qUnion([Q0]), "depth" : 35 * mm, "offsetDistance" : 25 * mm});
        }
    });
